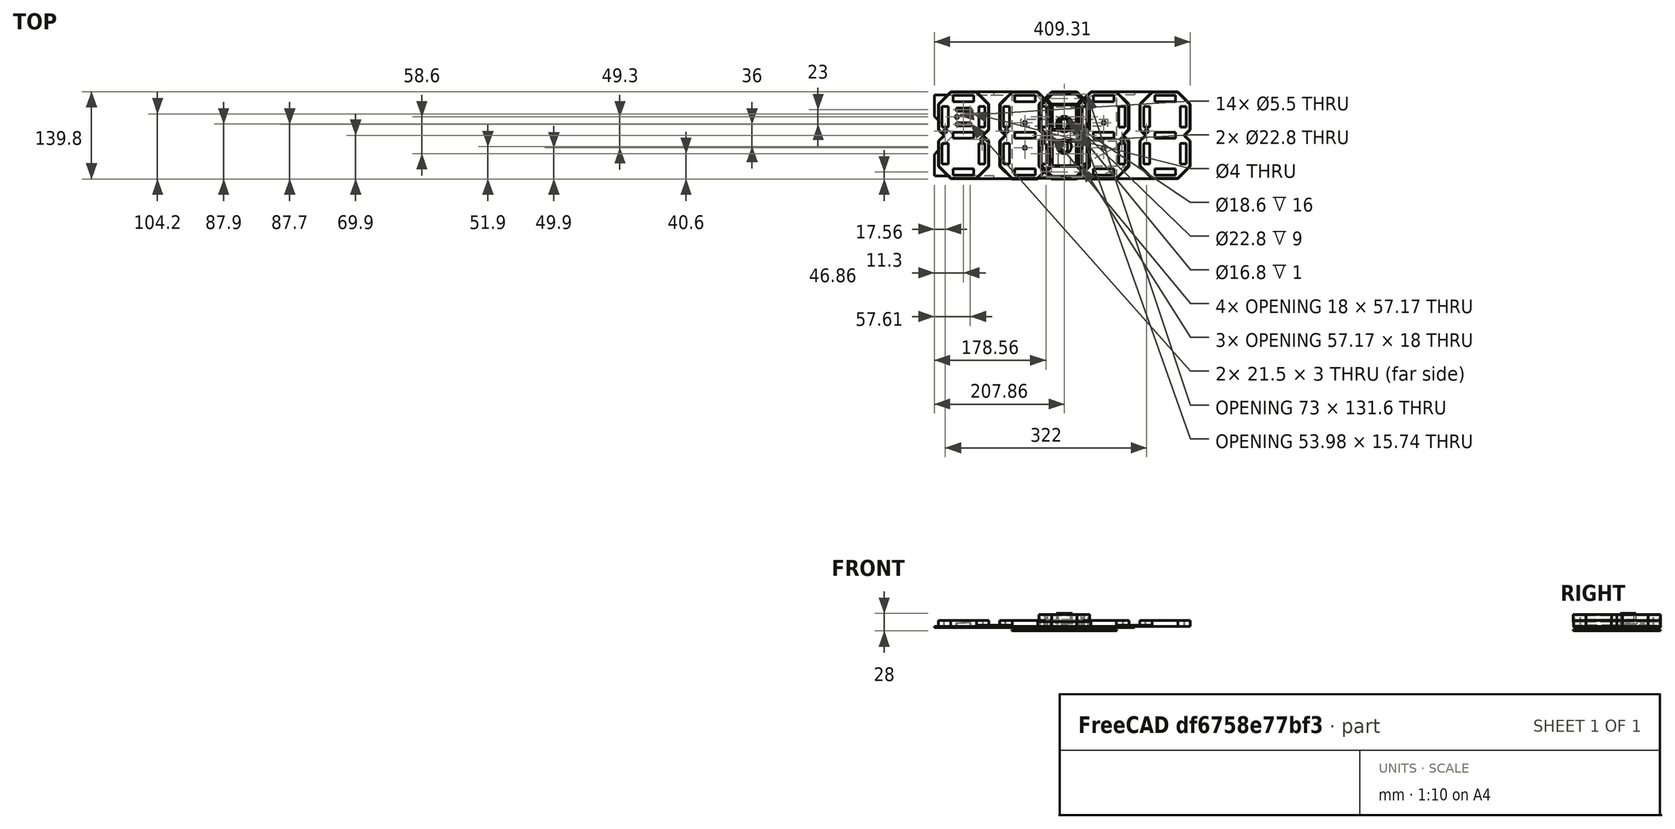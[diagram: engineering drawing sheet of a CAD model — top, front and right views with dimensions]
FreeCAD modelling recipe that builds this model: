
FCSTD DOCUMENT  (FreeCAD 0.19R24291 (Git))
Label: 7-segments-clock-17
License: All rights reserved
LicenseURL: http://en.wikipedia.org/wiki/All_rights_reserved
objects: Sketcher::SketchObject×33, PartDesign::Body×26, PartDesign::Pad×23, PartDesign::ShapeBinder×18, PartDesign::FeatureBase×11, PartDesign::Pocket×10, PartDesign::Thickness×5, Part::MultiFuse×4, PartDesign::Mirrored×4
note: 172 computed .brp shape members not serialized (recipe doc carries the construction recipe); baked Part::Feature solids carry a one-line shape summary decoded from their .brp

FEATURE [Sketcher::SketchObject] Sketch
  FullyConstrained = true
  MapMode = 5
  Support = -> [XY_Plane]
  sketch-geometry (14):
    g0: LineSegment StartX=-30 StartY=0 StartZ=0 EndX=-20 EndY=10 EndZ=0
    g1: LineSegment StartX=-20 StartY=10 StartZ=0 EndX=20 EndY=10 EndZ=0
    g2: LineSegment StartX=20 StartY=10 StartZ=0 EndX=30 EndY=0 EndZ=0
    g3: LineSegment StartX=30 StartY=0 StartZ=0 EndX=20 EndY=-10 EndZ=0
    g4: LineSegment StartX=20 StartY=-10 StartZ=0 EndX=-20 EndY=-10 EndZ=0
    g5: LineSegment StartX=-20 StartY=-10 StartZ=0 EndX=-30 EndY=0 EndZ=0
    g6: LineSegment StartX=-28.5858 StartY=5.3e-15 StartZ=0 EndX=-19.5858 EndY=9 EndZ=0
    g7: LineSegment StartX=-19.5858 StartY=9 StartZ=0 EndX=19.5858 EndY=9 EndZ=0
    g8: LineSegment StartX=19.5858 StartY=9 StartZ=0 EndX=28.5858 EndY=0 EndZ=0
    g9: LineSegment StartX=28.5858 StartY=0 StartZ=0 EndX=19.5858 EndY=-9 EndZ=0
    g10: LineSegment StartX=19.5858 StartY=-9 StartZ=0 EndX=-19.5858 EndY=-9 EndZ=0
    g11: LineSegment StartX=-19.5858 StartY=-9 StartZ=0 EndX=-28.5858 EndY=5.3e-15 EndZ=0
    g12: LineSegment StartX=-10 StartY=9 StartZ=0 EndX=-10 EndY=10 EndZ=0
    g13: LineSegment StartX=24.2426 StartY=4.34315 StartZ=0 EndX=24.9497 EndY=5.05025 EndZ=0
  constraints (41):
    c: PointOnObject(g0,g-1)
    c: Coincident(g0,g1)
    c: Horizontal(g1)
    c: Coincident(g1,g2)
    c: Coincident(g2,g3)
    c: Coincident(g3,g4)
    c: Horizontal(g4)
    c: Coincident(g4,g5)
    c: Coincident(g5,g0)
    c: Angle(g3,g4) = 2.35619
    c: Equal(g4,g1)
    c: Symmetric(g0,g3,g-1)
    c: Symmetric(g2,g0,g-2)
    c: Vertical(g3,g1)
    c: Coincident(g6,g7)
    c: Horizontal(g7)
    c: Coincident(g7,g8)
    c: Coincident(g8,g9)
    c: Coincident(g9,g10)
    c: Horizontal(g10)
    c: Coincident(g10,g11)
    c: Coincident(g11,g6)
    c: Angle(g9,g10) = 2.35619
    c: Equal(g10,g7)
    c: Vertical(g9,g7)
    c: Equal(g11,g6)
    c: Equal(g6,g8)
    c: Equal(g8,g9)
    c: Symmetric(g9,g6,g-1)
    c: PointOnObject(g12,g7)
    c: PointOnObject(g12,g1)
    c: Vertical(g12)
    c: Distance(g12) = 1
    c: PointOnObject(g13,g8)
    c: PointOnObject(g13,g2)
    c: Perpendicular(g13,g8)
    c: Equal(g12,g13)
    c: Distance(g0,g12) = 10
    c: Distance(g13,g1) = 7
    c: DistanceX(g0,g2) = 60
    c: DistanceY(g4,g0) = 20
FEATURE [PartDesign::Pad] Pad
  Direction = (1,1,1)
  Length = 18
  Length2 = 100
  Profile = -> Sketch
  Type = 0
FEATURE [PartDesign::Body] Body  label="original-middle"
  Group = -> [Sketch,Pad]
  Origin = -> Origin
  Tip = -> Pad
FEATURE [PartDesign::FeatureBase] Clone
  BaseFeature = -> Body
FEATURE [PartDesign::Body] Body001
  BaseFeature = -> Body
  Group = -> [Clone]
  Origin = -> Origin001
  Placement = pos=(-29.3,29.3,0) rot=(0,0,1;1.5708rad)
  Tip = -> Clone
FEATURE [PartDesign::FeatureBase] Clone001
  BaseFeature = -> Body
FEATURE [PartDesign::Body] Body002
  BaseFeature = -> Body
  Group = -> [Clone001]
  Origin = -> Origin002
  Placement = pos=(29.3,29.3,0) rot=(0,0,1;1.5708rad)
  Tip = -> Clone001
FEATURE [PartDesign::FeatureBase] Clone002
  BaseFeature = -> Body
FEATURE [PartDesign::Body] Body003
  BaseFeature = -> Body
  Group = -> [Clone002]
  Origin = -> Origin003
  Placement = pos=(0,58.6,0) rot=(0,0,1;0rad)
  Tip = -> Clone002
FEATURE [PartDesign::FeatureBase] Clone003
  BaseFeature = -> Body
FEATURE [PartDesign::Body] Body005
  BaseFeature = -> Body
  Group = -> [Clone003]
  Origin = -> Origin005
  Placement = pos=(-29.3,-29.3,0) rot=(0,0,1;1.5708rad)
  Tip = -> Clone003
FEATURE [PartDesign::FeatureBase] Clone004
  BaseFeature = -> Body
FEATURE [PartDesign::Body] Body006
  Group = -> [Clone004]
  Origin = -> Origin006
  Placement = pos=(0,-58.6,0) rot=(0,0,1;0rad)
  Tip = -> Clone004
FEATURE [PartDesign::FeatureBase] Clone005
  BaseFeature = -> Body
FEATURE [PartDesign::Body] Body007
  BaseFeature = -> Body
  Group = -> [Clone005]
  Origin = -> Origin007
  Placement = pos=(29.3,-29.3,0) rot=(0,0,1;1.5708rad)
  Tip = -> Clone005
FEATURE [Part::MultiFuse] Fusion  label="digit"
  Shapes = -> [Body,Body006,Body005,Body003,Body002,Body001,Body007]
FEATURE [PartDesign::ShapeBinder] ShapeBinder
  Support = -> [Fusion]
  TraceSupport = false
FEATURE [Sketcher::SketchObject] Sketch001
  ExternalGeometry = -> [ShapeBinder]
  FullyConstrained = false
  MapMode = 5
  Support = -> [XY_Plane008]
  sketch-geometry (19):
    g0: LineSegment StartX=-20.4763 StartY=69.75 StartZ=0 EndX=20.4763 EndY=69.75 EndZ=0
    g1: LineSegment StartX=20.4763 StartY=69.75 StartZ=0 EndX=40.45 EndY=49.7763 EndZ=0
    g2: LineSegment StartX=40.45 StartY=49.7763 StartZ=0 EndX=40.45 EndY=8.82365 EndZ=0
    g3: LineSegment StartX=40.45 StartY=8.82365 StartZ=0 EndX=31.6263 EndY=0 EndZ=0
    g4: LineSegment StartX=31.6263 StartY=0 StartZ=0 EndX=40.45 EndY=-8.82365 EndZ=0
    g5: LineSegment StartX=40.45 StartY=-8.82365 StartZ=0 EndX=40.45 EndY=-49.7763 EndZ=0
    g6: LineSegment StartX=40.45 StartY=-49.7763 StartZ=0 EndX=20.4763 EndY=-69.75 EndZ=0
    g7: LineSegment StartX=20.4763 StartY=-69.75 StartZ=0 EndX=-20.4763 EndY=-69.75 EndZ=0
    g8: LineSegment StartX=-20.4763 StartY=-69.75 StartZ=0 EndX=-40.45 EndY=-49.7763 EndZ=0
    g9: LineSegment StartX=-40.45 StartY=-49.7763 StartZ=0 EndX=-40.45 EndY=-8.82365 EndZ=0
    g10: LineSegment StartX=-40.45 StartY=-8.82365 StartZ=0 EndX=-31.6263 EndY=0 EndZ=0
    g11: LineSegment StartX=-31.6263 StartY=0 StartZ=0 EndX=-40.45 EndY=8.82365 EndZ=0
    g12: LineSegment StartX=-40.45 StartY=8.82365 StartZ=0 EndX=-40.45 EndY=49.7763 EndZ=0
    g13: LineSegment StartX=-40.45 StartY=49.7763 StartZ=0 EndX=-20.4763 EndY=69.75 EndZ=0
    g14: LineSegment StartX=-7.19333e+06 StartY=68.6 StartZ=0 EndX=-7.19333e+06 EndY=69.75 EndZ=0
    g15: LineSegment StartX=-7.19333e+06 StartY=-68.6 StartZ=0 EndX=-7.19333e+06 EndY=-69.75 EndZ=0
    g16: LineSegment StartX=-40.45 StartY=-3.5966e+06 StartZ=0 EndX=-39.3 EndY=-3.5966e+06 EndZ=0
    g17: LineSegment StartX=-33.1474 StartY=1.52109 StartZ=0 EndX=-32.3343 EndY=2.33426 EndZ=0
    g18: LineSegment StartX=-39.3 StartY=11.403 StartZ=0 EndX=-40.45 EndY=11.403 EndZ=0
  constraints (55):
    c: Horizontal(g0)
    c: Coincident(g0,g1)
    c: Coincident(g1,g2)
    c: Vertical(g2)
    c: Coincident(g2,g3)
    c: PointOnObject(g3,g-1)
    c: Coincident(g3,g4)
    c: Coincident(g4,g5)
    c: Vertical(g5)
    c: Coincident(g5,g6)
    c: Coincident(g6,g7)
    c: Horizontal(g7)
    c: Coincident(g7,g8)
    c: Coincident(g8,g9)
    c: Vertical(g9)
    c: Coincident(g9,g10)
    c: Coincident(g10,g11)
    c: Coincident(g11,g12)
    c: Vertical(g12)
    c: Coincident(g12,g13)
    c: Coincident(g13,g0)
    c: Equal(g13,g1)
    c: Equal(g1,g6)
    c: Equal(g6,g8)
    c: Equal(g9,g5)
    c: Equal(g5,g7)
    c: Equal(g7,g0)
    c: Equal(g0,g2)
    c: Equal(g2,g12)
    c: Equal(g11,g3)
    c: Vertical(g11,g9)
    c: Vertical(g4,g2)
    c: Symmetric(g3,g10,g-2)
    c: Symmetric(g4,g9,g-2)
    c: Angle(g11) = 2.35619
    c: Equal(g11,g10)
    c: PointOnObject(g14,g-3)
    c: Vertical(g14)
    c: PointOnObject(g15,g-12)
    c: PointOnObject(g15,g7)
    c: Vertical(g15)
    c: Equal(g15,g14)
    c: PointOnObject(g16,g12)
    c: PointOnObject(g16,g-5)
    c: Horizontal(g16)
    c: Equal(g14,g16)
    c: Angle(g13) = 0.785398
    c: PointOnObject(g17,g11)
    c: PointOnObject(g17,g-6)
    c: PointOnObject(g18,g-5)
    c: PointOnObject(g18,g12)
    c: Horizontal(g18)
    c: Perpendicular(g-6,g17)
    c: Equal(g17,g18)
    c: DistanceX(g18,g18) = 1.15
FEATURE [PartDesign::Pad] Pad001
  Direction = (1,1,1)
  Length = 10
  Length2 = 100
  Profile = -> Sketch001
  Type = 0
FEATURE [PartDesign::Thickness] Thickness
  Base = -> Pad001 [Face16]
  BaseFeature = -> Pad001
  Intersection = false
  Join = 0
  Mode = 0
  Reversed = true
  SupportTransform = false
  Value = 1
FEATURE [Sketcher::SketchObject] Sketch002
  ExternalGeometry = -> [ShapeBinder]
  FullyConstrained = true
  MapMode = 5
  Placement = pos=(0,0,1) rot=(0,0,1;0rad)
  Support = -> [Thickness]
  sketch-geometry (34):
    g0: LineSegment StartX=-29.3 StartY=48.8858 StartZ=0 EndX=-29.3 EndY=-48.8858 EndZ=0
    g1: LineSegment StartX=29.3 StartY=48.8858 StartZ=0 EndX=29.3 EndY=-48.8858 EndZ=0
    g2: LineSegment StartX=-19.5858 StartY=58.6 StartZ=0 EndX=19.5858 EndY=58.6 EndZ=0
    g3: LineSegment StartX=-19.5858 StartY=-58.6 StartZ=0 EndX=19.5858 EndY=-58.6 EndZ=0
    g4: LineSegment StartX=-16.5 StartY=63.6 StartZ=0 EndX=16.5 EndY=63.6 EndZ=0
    g5: LineSegment StartX=16.5 StartY=63.6 StartZ=0 EndX=16.5 EndY=53.6 EndZ=0
    g6: LineSegment StartX=16.5 StartY=53.6 StartZ=0 EndX=-16.5 EndY=53.6 EndZ=0
    g7: LineSegment StartX=-16.5 StartY=53.6 StartZ=0 EndX=-16.5 EndY=63.6 EndZ=0
    g8: LineSegment StartX=24.3 StartY=45.8 StartZ=0 EndX=34.3 EndY=45.8 EndZ=0
    g9: LineSegment StartX=34.3 StartY=45.8 StartZ=0 EndX=34.3 EndY=12.8 EndZ=0
    g10: LineSegment StartX=34.3 StartY=12.8 StartZ=0 EndX=24.3 EndY=12.8 EndZ=0
    g11: LineSegment StartX=24.3 StartY=12.8 StartZ=0 EndX=24.3 EndY=45.8 EndZ=0
    g12: LineSegment StartX=24.3 StartY=-12.8 StartZ=0 EndX=34.3 EndY=-12.8 EndZ=0
    g13: LineSegment StartX=34.3 StartY=-12.8 StartZ=0 EndX=34.3 EndY=-45.8 EndZ=0
    g14: LineSegment StartX=34.3 StartY=-45.8 StartZ=0 EndX=24.3 EndY=-45.8 EndZ=0
    g15: LineSegment StartX=24.3 StartY=-45.8 StartZ=0 EndX=24.3 EndY=-12.8 EndZ=0
    g16: LineSegment StartX=-34.3 StartY=-12.8 StartZ=0 EndX=-24.3 EndY=-12.8 EndZ=0
    g17: LineSegment StartX=-24.3 StartY=-12.8 StartZ=0 EndX=-24.3 EndY=-45.8 EndZ=0
    g18: LineSegment StartX=-24.3 StartY=-45.8 StartZ=0 EndX=-34.3 EndY=-45.8 EndZ=0
    g19: LineSegment StartX=-34.3 StartY=-45.8 StartZ=0 EndX=-34.3 EndY=-12.8 EndZ=0
    g20: LineSegment StartX=-16.5 StartY=-53.6 StartZ=0 EndX=16.5 EndY=-53.6 EndZ=0
    g21: LineSegment StartX=16.5 StartY=-53.6 StartZ=0 EndX=16.5 EndY=-63.6 EndZ=0
    g22: LineSegment StartX=16.5 StartY=-63.6 StartZ=0 EndX=-16.5 EndY=-63.6 EndZ=0
    g23: LineSegment StartX=-16.5 StartY=-63.6 StartZ=0 EndX=-16.5 EndY=-53.6 EndZ=0
    g24: LineSegment StartX=-34.3 StartY=45.8 StartZ=0 EndX=-24.3 EndY=45.8 EndZ=0
    g25: LineSegment StartX=-24.3 StartY=45.8 StartZ=0 EndX=-24.3 EndY=12.8 EndZ=0
    g26: LineSegment StartX=-24.3 StartY=12.8 StartZ=0 EndX=-34.3 EndY=12.8 EndZ=0
    g27: LineSegment StartX=-34.3 StartY=12.8 StartZ=0 EndX=-34.3 EndY=45.8 EndZ=0
    g28: LineSegment StartX=-16.5 StartY=5 StartZ=0 EndX=16.5 EndY=5 EndZ=0
    g29: LineSegment StartX=16.5 StartY=5 StartZ=0 EndX=16.5 EndY=-5 EndZ=0
    g30: LineSegment StartX=16.5 StartY=-5 StartZ=0 EndX=-16.5 EndY=-5 EndZ=0
    g31: LineSegment StartX=-16.5 StartY=-5 StartZ=0 EndX=-16.5 EndY=5 EndZ=0
    g32: LineSegment StartX=-38.3 StartY=-29.3 StartZ=0 EndX=38.3 EndY=-29.3 EndZ=0
    g33: LineSegment StartX=38.3 StartY=29.3 StartZ=0 EndX=-38.3 EndY=29.3 EndZ=0
  constraints (93):
    c: Symmetric(g-6,g-5,g0)
    c: Symmetric(g-4,g-3,g1)
    c: Horizontal(g1,g0)
    c: Horizontal(g0,g-6)
    c: Horizontal(g-14,g0)
    c: Horizontal(g0,g1)
    c: Horizontal(g2)
    c: Vertical(g3,g-16)
    c: Vertical(g3,g-15)
    c: Vertical(g-15,g2)
    c: Symmetric(g-15,g-16,g3)
    c: Symmetric(g-8,g-7,g2)
    c: Coincident(g4,g5)
    c: Coincident(g5,g6)
    c: Coincident(g6,g7)
    c: Coincident(g7,g4)
    c: Horizontal(g4)
    c: Horizontal(g6)
    c: Vertical(g7)
    c: Coincident(g8,g9)
    c: Coincident(g9,g10)
    c: Coincident(g10,g11)
    c: Coincident(g11,g8)
    c: Horizontal(g10)
    c: Vertical(g9)
    c: Coincident(g12,g13)
    c: Coincident(g13,g14)
    c: Coincident(g14,g15)
    c: Coincident(g15,g12)
    c: Horizontal(g12)
    c: Horizontal(g14)
    c: Vertical(g13)
    c: Vertical(g15)
    c: Coincident(g16,g17)
    c: Coincident(g17,g18)
    c: Coincident(g18,g19)
    c: Coincident(g19,g16)
    c: Horizontal(g16)
    c: Horizontal(g18)
    c: Vertical(g17)
    c: Coincident(g20,g21)
    c: Coincident(g21,g22)
    c: Coincident(g22,g23)
    c: Coincident(g23,g20)
    c: Horizontal(g22)
    c: Vertical(g21)
    c: DistanceX(g4,g4) = 33
    c: DistanceY(g7,g7) = 10
    c: Coincident(g24,g25)
    c: Coincident(g25,g26)
    c: Coincident(g26,g27)
    c: Coincident(g27,g24)
    c: Horizontal(g24)
    c: Vertical(g25)
    c: Vertical(g27)
    c: Equal(g6,g25)
    c: Equal(g25,g11)
    c: Equal(g11,g15)
    c: Equal(g15,g17)
    c: Equal(g17,g20)
    c: Equal(g7,g24)
    c: Equal(g24,g8)
    c: Equal(g8,g12)
    c: Equal(g12,g16)
    c: Equal(g16,g21)
    c: Coincident(g28,g29)
    c: Coincident(g29,g30)
    c: Coincident(g30,g31)
    c: Coincident(g31,g28)
    c: Horizontal(g30)
    c: Vertical(g29)
    c: Equal(g28,g4)
    c: Equal(g7,g31)
    c: Symmetric(g8,g8,g1)
    c: Vertical(g10,g12)
    c: Symmetric(g26,g25,g0)
    c: Vertical(g25,g16)
    c: Symmetric(g20,g22,g3)
    c: Symmetric(g20,g20,g-2)
    c: Vertical(g20,g5)
    c: Symmetric(g5,g4,g2)
    c: PointOnObject(g32,g-14)
    c: PointOnObject(g32,g-12)
    c: PointOnObject(g33,g-3)
    c: PointOnObject(g33,g-6)
    c: Symmetric(g-14,g-14,g32)
    c: Symmetric(g-6,g-6,g33)
    c: Symmetric(g8,g10,g33)
    c: Horizontal(g8,g24)
    c: Symmetric(g16,g18,g32)
    c: Horizontal(g16,g12)
    c: Symmetric(g28,g28,g-2)
    c: Symmetric(g30,g28,g-1)
FEATURE [PartDesign::Pad] Pad002
  BaseFeature = -> Thickness
  Direction = (1,1,1)
  Length = 0.3
  Length2 = 100
  Profile = -> Sketch002
  Type = 0
FEATURE [Sketcher::SketchObject] Sketch003
  ExternalGeometry = -> [ShapeBinder]
  FullyConstrained = true
  MapMode = 5
  Placement = pos=(0,0,1) rot=(0,0,1;0rad)
  Support = -> [Pad002]
  sketch-geometry (13):
    g0: LineSegment StartX=-19.3 StartY=29.3 StartZ=0 EndX=19.3 EndY=29.3 EndZ=0
    g1: Circle CenterX=-29.3 CenterY=6.71421 CenterZ=0 NormalX=0 NormalY=0 NormalZ=1 AngleXU=0 Radius=2.75
    g2: Circle CenterX=-10.75 CenterY=29.3 CenterZ=0 NormalX=0 NormalY=0 NormalZ=1 AngleXU=0 Radius=2.75
    g3: Circle CenterX=10.75 CenterY=34.3 CenterZ=0 NormalX=0 NormalY=0 NormalZ=1 AngleXU=0 Radius=2
    g4: Circle CenterX=29.3 CenterY=-6.71421 CenterZ=0 NormalX=0 NormalY=0 NormalZ=1 AngleXU=0 Radius=2.75
    g5: LineSegment StartX=-10.75 StartY=42.3 StartZ=0 EndX=10.75 EndY=42.3 EndZ=0
    g6: LineSegment StartX=10.75 StartY=42.3 StartZ=0 EndX=10.75 EndY=39.3 EndZ=0
    g7: LineSegment StartX=10.75 StartY=39.3 StartZ=0 EndX=-10.75 EndY=39.3 EndZ=0
    g8: LineSegment StartX=-10.75 StartY=39.3 StartZ=0 EndX=-10.75 EndY=42.3 EndZ=0
    g9: LineSegment StartX=-10.75 StartY=19.3 StartZ=0 EndX=10.75 EndY=19.3 EndZ=0
    g10: LineSegment StartX=10.75 StartY=19.3 StartZ=0 EndX=10.75 EndY=16.3 EndZ=0
    g11: LineSegment StartX=10.75 StartY=16.3 StartZ=0 EndX=-10.75 EndY=16.3 EndZ=0
    g12: LineSegment StartX=-10.75 StartY=16.3 StartZ=0 EndX=-10.75 EndY=19.3 EndZ=0
  constraints (38):
    c: Vertical(g0,g-3)
    c: Vertical(g0,g-3)
    c: Symmetric(g-3,g-4,g0)
    c: Radius(g1) = 2.75
    c: Equal(g1,g2)
    c: Equal(g2,g4)
    c: Radius(g3) = 2
    c: Coincident(g5,g6)
    c: Coincident(g6,g7)
    c: Coincident(g7,g8)
    c: Coincident(g8,g5)
    c: Horizontal(g5)
    c: Horizontal(g7)
    c: Vertical(g6)
    c: Vertical(g8)
    c: Coincident(g9,g10)
    c: Coincident(g10,g11)
    c: Coincident(g11,g12)
    c: Coincident(g12,g9)
    c: Horizontal(g11)
    c: Vertical(g10)
    c: Vertical(g12)
    c: Equal(g9,g7)
    c: Equal(g6,g10)
    c: Vertical(g1,g-6)
    c: Distance(g1,g-6) = 6
    c: Vertical(g4,g-8)
    c: Distance(g4,g-8) = 6
    c: DistanceY(g9,g0) = 10
    c: DistanceY(g0,g6) = 10
    c: Symmetric(g9,g9,g-2)
    c: Vertical(g6,g9)
    c: DistanceX(g5,g5) = 21.5
    c: DistanceY(g8,g8) = 3
    c: PointOnObject(g2,g0)
    c: Vertical(g3,g6)
    c: Vertical(g2,g7)
    c: DistanceY(g0,g3) = 5
FEATURE [PartDesign::Pocket] Pocket
  BaseFeature = -> Pad002
  Length = 5
  Length2 = 100
  Profile = -> Sketch003
  Type = 1
FEATURE [Sketcher::SketchObject] Sketch004
  ExternalGeometry = -> [Pocket]
  FullyConstrained = true
  MapMode = 5
  Placement = pos=(0,0,1) rot=(0,0,1;0rad)
  Support = -> [Pocket]
  sketch-geometry (16):
    g0: LineSegment StartX=-10.75 StartY=42.3 StartZ=0 EndX=10.75 EndY=42.3 EndZ=0
    g1: LineSegment StartX=10.75 StartY=42.3 StartZ=0 EndX=10.75 EndY=39.3 EndZ=0
    g2: LineSegment StartX=10.75 StartY=39.3 StartZ=0 EndX=-10.75 EndY=39.3 EndZ=0
    g3: LineSegment StartX=-10.75 StartY=39.3 StartZ=0 EndX=-10.75 EndY=42.3 EndZ=0
    g4: LineSegment StartX=-10.75 StartY=19.3 StartZ=0 EndX=10.75 EndY=19.3 EndZ=0
    g5: LineSegment StartX=10.75 StartY=19.3 StartZ=0 EndX=10.75 EndY=16.3 EndZ=0
    g6: LineSegment StartX=10.75 StartY=16.3 StartZ=0 EndX=-10.75 EndY=16.3 EndZ=0
    g7: LineSegment StartX=-10.75 StartY=16.3 StartZ=0 EndX=-10.75 EndY=19.3 EndZ=0
    g8: LineSegment StartX=-11.75 StartY=43.3 StartZ=0 EndX=11.75 EndY=43.3 EndZ=0
    g9: LineSegment StartX=11.75 StartY=43.3 StartZ=0 EndX=11.75 EndY=38.3 EndZ=0
    g10: LineSegment StartX=11.75 StartY=38.3 StartZ=0 EndX=-11.75 EndY=38.3 EndZ=0
    g11: LineSegment StartX=-11.75 StartY=38.3 StartZ=0 EndX=-11.75 EndY=43.3 EndZ=0
    g12: LineSegment StartX=-11.75 StartY=20.3 StartZ=0 EndX=11.75 EndY=20.3 EndZ=0
    g13: LineSegment StartX=11.75 StartY=20.3 StartZ=0 EndX=11.75 EndY=15.3 EndZ=0
    g14: LineSegment StartX=11.75 StartY=15.3 StartZ=0 EndX=-11.75 EndY=15.3 EndZ=0
    g15: LineSegment StartX=-11.75 StartY=15.3 StartZ=0 EndX=-11.75 EndY=20.3 EndZ=0
  constraints (42):
    c: Coincident(g0,g1)
    c: Coincident(g1,g2)
    c: Coincident(g2,g3)
    c: Coincident(g3,g0)
    c: Horizontal(g0)
    c: Horizontal(g2)
    c: Vertical(g1)
    c: Vertical(g3)
    c: Coincident(g0,g-3)
    c: Coincident(g1,g-4)
    c: Coincident(g4,g5)
    c: Coincident(g5,g6)
    c: Coincident(g6,g7)
    c: Coincident(g7,g4)
    c: Horizontal(g4)
    c: Horizontal(g6)
    c: Vertical(g5)
    c: Vertical(g7)
    c: Coincident(g4,g-5)
    c: Coincident(g5,g-6)
    c: Coincident(g8,g9)
    c: Coincident(g9,g10)
    c: Coincident(g10,g11)
    c: Coincident(g11,g8)
    c: Horizontal(g8)
    c: Vertical(g9)
    c: Vertical(g11)
    c: Coincident(g12,g13)
    c: Coincident(g13,g14)
    c: Coincident(g14,g15)
    c: Coincident(g15,g12)
    c: Horizontal(g14)
    c: Vertical(g13)
    c: Vertical(g15)
    c: Equal(g12,g10)
    c: Equal(g9,g13)
    c: Symmetric(g12,g12,g-2)
    c: Symmetric(g10,g9,g-2)
    c: DistanceY(g0,g8) = 1
    c: DistanceY(g9,g1) = 1
    c: DistanceX(g1,g9) = 1
    c: DistanceY(g4,g12) = 1
FEATURE [PartDesign::Pad] Pad003
  BaseFeature = -> Pocket
  Direction = (1,1,1)
  Length = 5
  Length2 = 100
  Profile = -> Sketch004
  Type = 0
FEATURE [PartDesign::Body] Body008  label="back-esp"
  Group = -> [ShapeBinder,Sketch001,Pad001,Thickness,Sketch002,Pad002,Sketch003,Pocket,Sketch004,Pad003]
  Origin = -> Origin008
  Tip = -> Pad003
FEATURE [PartDesign::ShapeBinder] ShapeBinder001
  Support = -> [Body]
  TraceSupport = false
FEATURE [Sketcher::SketchObject] Sketch005
  ExternalGeometry = -> [ShapeBinder001]
  FullyConstrained = false
  MapMode = 5
  Support = -> [XY_Plane009]
  sketch-geometry (8):
    g0: LineSegment StartX=-19.5319 StartY=8.87 StartZ=0 EndX=19.5319 EndY=8.87 EndZ=0
    g1: LineSegment StartX=19.5319 StartY=8.87 StartZ=0 EndX=28.4019 EndY=0 EndZ=0
    g2: LineSegment StartX=28.4019 StartY=0 StartZ=0 EndX=19.5319 EndY=-8.87 EndZ=0
    g3: LineSegment StartX=19.5319 StartY=-8.87 StartZ=0 EndX=-19.5319 EndY=-8.87 EndZ=0
    g4: LineSegment StartX=-19.5319 StartY=-8.87 StartZ=0 EndX=-28.4019 EndY=0 EndZ=0
    g5: LineSegment StartX=-28.4019 StartY=0 StartZ=0 EndX=-19.5319 EndY=8.87 EndZ=0
    g6: LineSegment StartX=6.84283 StartY=8.87 StartZ=0 EndX=6.84283 EndY=9 EndZ=0
    g7: LineSegment StartX=22.9862 StartY=5.41571 StartZ=0 EndX=23.0782 EndY=5.50763 EndZ=0
  constraints (21):
    c: Coincident(g0,g1)
    c: PointOnObject(g1,g-1)
    c: Coincident(g1,g2)
    c: Coincident(g2,g3)
    c: Horizontal(g3)
    c: Coincident(g3,g4)
    c: Coincident(g4,g5)
    c: Equal(g0,g3)
    c: Symmetric(g4,g1,g-2)
    c: Symmetric(g2,g0,g-1)
    c: Angle(g5) = 0.785398
    c: PointOnObject(g6,g0)
    c: PointOnObject(g6,g-3)
    c: Vertical(g6)
    c: DistanceY(g6,g6) = 0.13
    c: PointOnObject(g7,g1)
    c: PointOnObject(g7,g-7)
    c: Perpendicular(g1,g7)
    c: Equal(g7,g6)
    c: Coincident(g0,g5)
    c: Symmetric(g0,g0,g-2)
FEATURE [PartDesign::Pad] Pad004
  Direction = (1,1,1)
  Length = 18
  Length2 = 100
  Profile = -> Sketch005
  Type = 0
FEATURE [Sketcher::SketchObject] Sketch006
  ExternalGeometry = -> [Pad004]
  FullyConstrained = false
  MapMode = 5
  Placement = pos=(0,0,18) rot=(0,0,1;0rad)
  Support = -> [Pad004]
  sketch-geometry (8):
    g0: LineSegment StartX=-19.1177 StartY=7.87 StartZ=0 EndX=19.1177 EndY=7.87 EndZ=0
    g1: LineSegment StartX=19.1177 StartY=7.87 StartZ=0 EndX=26.9877 EndY=-9e-16 EndZ=0
    g2: LineSegment StartX=26.9877 StartY=0 StartZ=0 EndX=19.1177 EndY=-7.87 EndZ=0
    g3: LineSegment StartX=19.1177 StartY=-7.87 StartZ=0 EndX=-19.1177 EndY=-7.87 EndZ=0
    g4: LineSegment StartX=-19.1177 StartY=-7.87 StartZ=0 EndX=-26.9877 EndY=-9e-16 EndZ=0
    g5: LineSegment StartX=-26.9877 StartY=0 StartZ=0 EndX=-19.1177 EndY=7.87 EndZ=0
    g6: LineSegment StartX=5.64393 StartY=7.87 StartZ=0 EndX=5.64393 EndY=8.87 EndZ=0
    g7: LineSegment StartX=23.5274 StartY=3.46031 StartZ=0 EndX=24.2345 EndY=4.16742 EndZ=0
  constraints (22):
    c: Horizontal(g0)
    c: Coincident(g0,g1)
    c: PointOnObject(g1,g-1)
    c: Coincident(g1,g2)
    c: Coincident(g2,g3)
    c: Horizontal(g3)
    c: Coincident(g3,g4)
    c: Coincident(g4,g5)
    c: Coincident(g5,g0)
    c: Symmetric(g1,g4,g-2)
    c: Symmetric(g2,g0,g-1)
    c: Equal(g2,g5)
    c: Angle(g5) = 0.785398
    c: Vertical(g0,g3)
    c: PointOnObject(g6,g0)
    c: PointOnObject(g6,g-3)
    c: Vertical(g6)
    c: PointOnObject(g7,g1)
    c: PointOnObject(g7,g-8)
    c: Perpendicular(g1,g7)
    c: Equal(g6,g7)
    c: DistanceY(g6,g6) = 1
FEATURE [PartDesign::Pocket] Pocket001
  BaseFeature = -> Pad004
  Length = 5
  Length2 = 100
  Profile = -> Sketch006
  Type = 1
FEATURE [PartDesign::Body] Body009  label="single-segment"
  Group = -> [ShapeBinder001,Sketch005,Pad004,Sketch006,Pocket001]
  Origin = -> Origin009
  Tip = -> Pocket001
FEATURE [PartDesign::ShapeBinder] ShapeBinder002
  Support = -> [Fusion]
  TraceSupport = false
FEATURE [Sketcher::SketchObject] Sketch008
  ExternalGeometry = -> [ShapeBinder002]
  FullyConstrained = false
  MapMode = 5
  Support = -> [XY_Plane017]
  sketch-geometry (19):
    g0: LineSegment StartX=-20.4971 StartY=69.8 StartZ=0 EndX=20.4971 EndY=69.8 EndZ=0
    g1: LineSegment StartX=20.4971 StartY=69.8 StartZ=0 EndX=40.5 EndY=49.7971 EndZ=0
    g2: LineSegment StartX=40.5 StartY=49.7971 StartZ=0 EndX=40.5 EndY=8.80294 EndZ=0
    g3: LineSegment StartX=40.5 StartY=8.80294 StartZ=0 EndX=31.6971 EndY=0 EndZ=0
    g4: LineSegment StartX=31.6971 StartY=0 StartZ=0 EndX=40.5 EndY=-8.80294 EndZ=0
    g5: LineSegment StartX=40.5 StartY=-8.80294 StartZ=0 EndX=40.5 EndY=-49.7971 EndZ=0
    g6: LineSegment StartX=40.5 StartY=-49.7971 StartZ=0 EndX=20.4971 EndY=-69.8 EndZ=0
    g7: LineSegment StartX=20.4971 StartY=-69.8 StartZ=0 EndX=-20.4971 EndY=-69.8 EndZ=0
    g8: LineSegment StartX=-20.4971 StartY=-69.8 StartZ=0 EndX=-40.5 EndY=-49.7971 EndZ=0
    g9: LineSegment StartX=-40.5 StartY=-49.7971 StartZ=0 EndX=-40.5 EndY=-8.80294 EndZ=0
    g10: LineSegment StartX=-40.5 StartY=-8.80294 StartZ=0 EndX=-31.6971 EndY=0 EndZ=0
    g11: LineSegment StartX=-31.6971 StartY=0 StartZ=0 EndX=-40.5 EndY=8.80294 EndZ=0
    g12: LineSegment StartX=-40.5 StartY=8.80294 StartZ=0 EndX=-40.5 EndY=49.7971 EndZ=0
    g13: LineSegment StartX=-40.5 StartY=49.7971 StartZ=0 EndX=-20.4971 EndY=69.8 EndZ=0
    g14: LineSegment StartX=-7.19333e+06 StartY=68.6 StartZ=0 EndX=-7.19333e+06 EndY=69.8 EndZ=0
    g15: LineSegment StartX=-7.19333e+06 StartY=-68.6 StartZ=0 EndX=-7.19333e+06 EndY=-69.8 EndZ=0
    g16: LineSegment StartX=-40.5 StartY=-3.5966e+06 StartZ=0 EndX=-39.3 EndY=-3.5966e+06 EndZ=0
    g17: LineSegment StartX=34.9315 StartY=3.23442 StartZ=0 EndX=34.083 EndY=4.08295 EndZ=0
    g18: LineSegment StartX=40.5 StartY=11.0092 StartZ=0 EndX=39.3 EndY=11.0092 EndZ=0
  constraints (55):
    c: Horizontal(g0)
    c: Coincident(g0,g1)
    c: Coincident(g1,g2)
    c: Vertical(g2)
    c: Coincident(g2,g3)
    c: PointOnObject(g3,g-1)
    c: Coincident(g3,g4)
    c: Coincident(g4,g5)
    c: Vertical(g5)
    c: Coincident(g5,g6)
    c: Coincident(g6,g7)
    c: Horizontal(g7)
    c: Coincident(g7,g8)
    c: Coincident(g8,g9)
    c: Vertical(g9)
    c: Coincident(g9,g10)
    c: Coincident(g10,g11)
    c: Coincident(g11,g12)
    c: Vertical(g12)
    c: Coincident(g12,g13)
    c: Coincident(g13,g0)
    c: Equal(g13,g1)
    c: Equal(g1,g6)
    c: Equal(g6,g8)
    c: Equal(g9,g5)
    c: Equal(g5,g7)
    c: Equal(g7,g0)
    c: Equal(g0,g2)
    c: Equal(g2,g12)
    c: Equal(g11,g3)
    c: Vertical(g11,g9)
    c: Vertical(g4,g2)
    c: Symmetric(g3,g10,g-2)
    c: Symmetric(g4,g9,g-2)
    c: Angle(g11) = 2.35619
    c: Equal(g11,g10)
    c: PointOnObject(g14,g-3)
    c: Vertical(g14)
    c: PointOnObject(g15,g-12)
    c: PointOnObject(g15,g7)
    c: Vertical(g15)
    c: Equal(g15,g14)
    c: PointOnObject(g16,g12)
    c: PointOnObject(g16,g-5)
    c: Horizontal(g16)
    c: Equal(g14,g16)
    c: Angle(g13) = 0.785398
    c: PointOnObject(g17,g3)
    c: PointOnObject(g18,g2)
    c: Horizontal(g18)
    c: Perpendicular(g-9,g17)
    c: Equal(g18,g17)
    c: PointOnObject(g18,g-4)
    c: PointOnObject(g17,g-9)
    c: DistanceX(g18,g18) = 1.2
FEATURE [PartDesign::Pad] Pad006
  Direction = (1,1,1)
  Length = 11.5
  Length2 = 100
  Profile = -> Sketch008
  Type = 0
FEATURE [PartDesign::Thickness] Thickness001
  Base = -> Pad006 [Face16]
  BaseFeature = -> Pad006
  Intersection = false
  Join = 0
  Mode = 0
  Reversed = true
  SupportTransform = false
  Value = 1
FEATURE [Sketcher::SketchObject] Sketch009
  ExternalGeometry = -> [Thickness001]
  FullyConstrained = false
  MapMode = 5
  Placement = pos=(0,0,1) rot=(0,0,1;0rad)
  Support = -> [Thickness001]
  sketch-geometry (17):
    g0: LineSegment StartX=-18.8402 StartY=65.8 StartZ=0 EndX=18.8402 EndY=65.8 EndZ=0
    g1: LineSegment StartX=18.8402 StartY=65.8 StartZ=0 EndX=36.5 EndY=48.1402 EndZ=0
    g2: LineSegment StartX=36.5 StartY=48.1402 StartZ=0 EndX=36.5 EndY=10.4598 EndZ=0
    g3: LineSegment StartX=36.5 StartY=10.4598 StartZ=0 EndX=26.0402 EndY=0 EndZ=0
    g4: LineSegment StartX=26.0402 StartY=0 StartZ=0 EndX=36.5 EndY=-10.4598 EndZ=0
    g5: LineSegment StartX=36.5 StartY=-10.4598 StartZ=0 EndX=36.5 EndY=-48.1402 EndZ=0
    g6: LineSegment StartX=36.5 StartY=-48.1402 StartZ=0 EndX=18.8402 EndY=-65.8 EndZ=0
    g7: LineSegment StartX=18.8402 StartY=-65.8 StartZ=0 EndX=-18.8402 EndY=-65.8 EndZ=0
    g8: LineSegment StartX=-18.8402 StartY=-65.8 StartZ=0 EndX=-36.5 EndY=-48.1402 EndZ=0
    g9: LineSegment StartX=-36.5 StartY=-48.1402 StartZ=0 EndX=-36.5 EndY=-10.4598 EndZ=0
    g10: LineSegment StartX=-36.5 StartY=-10.4598 StartZ=0 EndX=-26.0402 EndY=0 EndZ=0
    g11: LineSegment StartX=-26.0402 StartY=0 StartZ=0 EndX=-36.5 EndY=10.4598 EndZ=0
    g12: LineSegment StartX=-36.5 StartY=10.4598 StartZ=0 EndX=-36.5 EndY=48.1402 EndZ=0
    g13: LineSegment StartX=-36.5 StartY=48.1402 StartZ=0 EndX=-18.8402 EndY=65.8 EndZ=0
    g14: LineSegment StartX=36.5 StartY=19.7121 StartZ=0 EndX=39.5 EndY=19.7121 EndZ=0
    g15: LineSegment StartX=32.3726 StartY=6.33239 StartZ=0 EndX=34.4939 EndY=4.21107 EndZ=0
    g16: LineSegment StartX=4.90979 StartY=65.8 StartZ=0 EndX=4.90979 EndY=68.8 EndZ=0
  constraints (48):
    c: Horizontal(g0)
    c: Coincident(g0,g1)
    c: Coincident(g1,g2)
    c: Vertical(g2)
    c: Coincident(g2,g3)
    c: PointOnObject(g3,g-1)
    c: Coincident(g3,g4)
    c: Coincident(g4,g5)
    c: Vertical(g5)
    c: Coincident(g5,g6)
    c: Coincident(g6,g7)
    c: Horizontal(g7)
    c: Coincident(g7,g8)
    c: Coincident(g8,g9)
    c: Vertical(g9)
    c: Coincident(g9,g10)
    c: Coincident(g10,g11)
    c: Coincident(g11,g12)
    c: Vertical(g12)
    c: Coincident(g12,g13)
    c: Coincident(g13,g0)
    c: Equal(g5,g2)
    c: Equal(g2,g0)
    c: Equal(g0,g12)
    c: Equal(g12,g9)
    c: Equal(g9,g7)
    c: Equal(g8,g6)
    c: Equal(g6,g1)
    c: Equal(g1,g13)
    c: Angle(g13) = 0.785398
    c: Symmetric(g10,g3,g-2)
    c: Symmetric(g9,g4,g-2)
    c: Vertical(g9,g11)
    c: Horizontal(g1,g12)
    c: Symmetric(g4,g2,g-1)
    c: Angle(g10) = 0.785398
    c: PointOnObject(g14,g2)
    c: PointOnObject(g14,g-13)
    c: Horizontal(g14)
    c: PointOnObject(g15,g3)
    c: PointOnObject(g15,g-12)
    c: Perpendicular(g-12,g15)
    c: Equal(g15,g14)
    c: Distance(g14) = 3
    c: PointOnObject(g16,g0)
    c: PointOnObject(g16,g-3)
    c: Vertical(g16)
    c: Equal(g16,g14)
FEATURE [PartDesign::Pocket] Pocket002
  BaseFeature = -> Thickness001
  Length = 5
  Length2 = 100
  Profile = -> Sketch009
  Type = 0
FEATURE [PartDesign::Body] Body017  label="cover"
  Group = -> [ShapeBinder002,Sketch008,Pad006,Thickness001,Sketch009,Pocket002]
  Origin = -> Origin017
  Placement = pos=(-2e-15,0,19) rot=(0,1,0;3.14159rad)
  Tip = -> Pocket002
FEATURE [PartDesign::ShapeBinder] ShapeBinder003
  Support = -> [Fusion]
  TraceSupport = false
FEATURE [Sketcher::SketchObject] Sketch011
  ExternalGeometry = -> [ShapeBinder003]
  FullyConstrained = false
  MapMode = 5
  Support = -> [XY_Plane025]
  sketch-geometry (19):
    g0: LineSegment StartX=-20.4763 StartY=69.75 StartZ=0 EndX=20.4763 EndY=69.75 EndZ=0
    g1: LineSegment StartX=20.4763 StartY=69.75 StartZ=0 EndX=40.45 EndY=49.7763 EndZ=0
    g2: LineSegment StartX=40.45 StartY=49.7763 StartZ=0 EndX=40.45 EndY=8.82365 EndZ=0
    g3: LineSegment StartX=40.45 StartY=8.82365 StartZ=0 EndX=31.6263 EndY=0 EndZ=0
    g4: LineSegment StartX=31.6263 StartY=0 StartZ=0 EndX=40.45 EndY=-8.82365 EndZ=0
    g5: LineSegment StartX=40.45 StartY=-8.82365 StartZ=0 EndX=40.45 EndY=-49.7763 EndZ=0
    g6: LineSegment StartX=40.45 StartY=-49.7763 StartZ=0 EndX=20.4763 EndY=-69.75 EndZ=0
    g7: LineSegment StartX=20.4763 StartY=-69.75 StartZ=0 EndX=-20.4763 EndY=-69.75 EndZ=0
    g8: LineSegment StartX=-20.4763 StartY=-69.75 StartZ=0 EndX=-40.45 EndY=-49.7763 EndZ=0
    g9: LineSegment StartX=-40.45 StartY=-49.7763 StartZ=0 EndX=-40.45 EndY=-8.82365 EndZ=0
    g10: LineSegment StartX=-40.45 StartY=-8.82365 StartZ=0 EndX=-31.6263 EndY=0 EndZ=0
    g11: LineSegment StartX=-31.6263 StartY=0 StartZ=0 EndX=-40.45 EndY=8.82365 EndZ=0
    g12: LineSegment StartX=-40.45 StartY=8.82365 StartZ=0 EndX=-40.45 EndY=49.7763 EndZ=0
    g13: LineSegment StartX=-40.45 StartY=49.7763 StartZ=0 EndX=-20.4763 EndY=69.75 EndZ=0
    g14: LineSegment StartX=-7.19333e+06 StartY=68.6 StartZ=0 EndX=-7.19333e+06 EndY=69.75 EndZ=0
    g15: LineSegment StartX=-7.19333e+06 StartY=-68.6 StartZ=0 EndX=-7.19333e+06 EndY=-69.75 EndZ=0
    g16: LineSegment StartX=-40.45 StartY=-3.5966e+06 StartZ=0 EndX=-39.3 EndY=-3.5966e+06 EndZ=0
    g17: LineSegment StartX=-37.2391 StartY=5.61277 StartZ=0 EndX=-36.4259 EndY=6.42595 EndZ=0
    g18: LineSegment StartX=-39.3 StartY=10.8091 StartZ=0 EndX=-40.45 EndY=10.8091 EndZ=0
  constraints (55):
    c: Horizontal(g0)
    c: Coincident(g0,g1)
    c: Coincident(g1,g2)
    c: Vertical(g2)
    c: Coincident(g2,g3)
    c: PointOnObject(g3,g-1)
    c: Coincident(g3,g4)
    c: Coincident(g4,g5)
    c: Vertical(g5)
    c: Coincident(g5,g6)
    c: Coincident(g6,g7)
    c: Horizontal(g7)
    c: Coincident(g7,g8)
    c: Coincident(g8,g9)
    c: Vertical(g9)
    c: Coincident(g9,g10)
    c: Coincident(g10,g11)
    c: Coincident(g11,g12)
    c: Vertical(g12)
    c: Coincident(g12,g13)
    c: Coincident(g13,g0)
    c: Equal(g13,g1)
    c: Equal(g1,g6)
    c: Equal(g6,g8)
    c: Equal(g9,g5)
    c: Equal(g5,g7)
    c: Equal(g7,g0)
    c: Equal(g0,g2)
    c: Equal(g2,g12)
    c: Equal(g11,g3)
    c: Vertical(g11,g9)
    c: Vertical(g4,g2)
    c: Symmetric(g3,g10,g-2)
    c: Symmetric(g4,g9,g-2)
    c: Angle(g11) = 2.35619
    c: Equal(g11,g10)
    c: PointOnObject(g14,g-3)
    c: Vertical(g14)
    c: PointOnObject(g15,g-12)
    c: PointOnObject(g15,g7)
    c: Vertical(g15)
    c: Equal(g15,g14)
    c: PointOnObject(g16,g12)
    c: PointOnObject(g16,g-5)
    c: Horizontal(g16)
    c: Equal(g14,g16)
    c: Angle(g13) = 0.785398
    c: PointOnObject(g17,g11)
    c: PointOnObject(g17,g-6)
    c: PointOnObject(g18,g-5)
    c: PointOnObject(g18,g12)
    c: Horizontal(g18)
    c: Perpendicular(g-6,g17)
    c: Equal(g17,g18)
    c: DistanceX(g18,g18) = 1.15
FEATURE [PartDesign::Pad] Pad008
  Direction = (1,1,1)
  Length = 10
  Length2 = 100
  Profile = -> Sketch011
  Type = 0
FEATURE [PartDesign::Thickness] Thickness002
  Base = -> Pad008 [Face16]
  BaseFeature = -> Pad008
  Intersection = false
  Join = 0
  Mode = 0
  Reversed = true
  SupportTransform = false
  Value = 1
FEATURE [Sketcher::SketchObject] Sketch012
  ExternalGeometry = -> [ShapeBinder003]
  FullyConstrained = true
  MapMode = 5
  Placement = pos=(0,0,1) rot=(0,0,1;0rad)
  Support = -> [Thickness002]
  sketch-geometry (34):
    g0: LineSegment StartX=-29.3 StartY=48.8858 StartZ=0 EndX=-29.3 EndY=-48.8858 EndZ=0
    g1: LineSegment StartX=29.3 StartY=48.8858 StartZ=0 EndX=29.3 EndY=-48.8858 EndZ=0
    g2: LineSegment StartX=-19.5858 StartY=58.6 StartZ=0 EndX=19.5858 EndY=58.6 EndZ=0
    g3: LineSegment StartX=-19.5858 StartY=-58.6 StartZ=0 EndX=19.5858 EndY=-58.6 EndZ=0
    g4: LineSegment StartX=-16.5 StartY=63.6 StartZ=0 EndX=16.5 EndY=63.6 EndZ=0
    g5: LineSegment StartX=16.5 StartY=63.6 StartZ=0 EndX=16.5 EndY=53.6 EndZ=0
    g6: LineSegment StartX=16.5 StartY=53.6 StartZ=0 EndX=-16.5 EndY=53.6 EndZ=0
    g7: LineSegment StartX=-16.5 StartY=53.6 StartZ=0 EndX=-16.5 EndY=63.6 EndZ=0
    g8: LineSegment StartX=24.3 StartY=45.8 StartZ=0 EndX=34.3 EndY=45.8 EndZ=0
    g9: LineSegment StartX=34.3 StartY=45.8 StartZ=0 EndX=34.3 EndY=12.8 EndZ=0
    g10: LineSegment StartX=34.3 StartY=12.8 StartZ=0 EndX=24.3 EndY=12.8 EndZ=0
    g11: LineSegment StartX=24.3 StartY=12.8 StartZ=0 EndX=24.3 EndY=45.8 EndZ=0
    g12: LineSegment StartX=24.3 StartY=-12.8 StartZ=0 EndX=34.3 EndY=-12.8 EndZ=0
    g13: LineSegment StartX=34.3 StartY=-12.8 StartZ=0 EndX=34.3 EndY=-45.8 EndZ=0
    g14: LineSegment StartX=34.3 StartY=-45.8 StartZ=0 EndX=24.3 EndY=-45.8 EndZ=0
    g15: LineSegment StartX=24.3 StartY=-45.8 StartZ=0 EndX=24.3 EndY=-12.8 EndZ=0
    g16: LineSegment StartX=-34.3 StartY=-12.8 StartZ=0 EndX=-24.3 EndY=-12.8 EndZ=0
    g17: LineSegment StartX=-24.3 StartY=-12.8 StartZ=0 EndX=-24.3 EndY=-45.8 EndZ=0
    g18: LineSegment StartX=-24.3 StartY=-45.8 StartZ=0 EndX=-34.3 EndY=-45.8 EndZ=0
    g19: LineSegment StartX=-34.3 StartY=-45.8 StartZ=0 EndX=-34.3 EndY=-12.8 EndZ=0
    g20: LineSegment StartX=-16.5 StartY=-53.6 StartZ=0 EndX=16.5 EndY=-53.6 EndZ=0
    g21: LineSegment StartX=16.5 StartY=-53.6 StartZ=0 EndX=16.5 EndY=-63.6 EndZ=0
    g22: LineSegment StartX=16.5 StartY=-63.6 StartZ=0 EndX=-16.5 EndY=-63.6 EndZ=0
    g23: LineSegment StartX=-16.5 StartY=-63.6 StartZ=0 EndX=-16.5 EndY=-53.6 EndZ=0
    g24: LineSegment StartX=-34.3 StartY=45.8 StartZ=0 EndX=-24.3 EndY=45.8 EndZ=0
    g25: LineSegment StartX=-24.3 StartY=45.8 StartZ=0 EndX=-24.3 EndY=12.8 EndZ=0
    g26: LineSegment StartX=-24.3 StartY=12.8 StartZ=0 EndX=-34.3 EndY=12.8 EndZ=0
    g27: LineSegment StartX=-34.3 StartY=12.8 StartZ=0 EndX=-34.3 EndY=45.8 EndZ=0
    g28: LineSegment StartX=-16.5 StartY=5 StartZ=0 EndX=16.5 EndY=5 EndZ=0
    g29: LineSegment StartX=16.5 StartY=5 StartZ=0 EndX=16.5 EndY=-5 EndZ=0
    g30: LineSegment StartX=16.5 StartY=-5 StartZ=0 EndX=-16.5 EndY=-5 EndZ=0
    g31: LineSegment StartX=-16.5 StartY=-5 StartZ=0 EndX=-16.5 EndY=5 EndZ=0
    g32: LineSegment StartX=-38.3 StartY=-29.3 StartZ=0 EndX=38.3 EndY=-29.3 EndZ=0
    g33: LineSegment StartX=38.3 StartY=29.3 StartZ=0 EndX=-38.3 EndY=29.3 EndZ=0
  constraints (93):
    c: Symmetric(g-6,g-5,g0)
    c: Symmetric(g-4,g-3,g1)
    c: Horizontal(g1,g0)
    c: Horizontal(g0,g-6)
    c: Horizontal(g-14,g0)
    c: Horizontal(g0,g1)
    c: Horizontal(g2)
    c: Vertical(g3,g-16)
    c: Vertical(g3,g-15)
    c: Vertical(g-15,g2)
    c: Symmetric(g-15,g-16,g3)
    c: Symmetric(g-8,g-7,g2)
    c: Coincident(g4,g5)
    c: Coincident(g5,g6)
    c: Coincident(g6,g7)
    c: Coincident(g7,g4)
    c: Horizontal(g4)
    c: Horizontal(g6)
    c: Vertical(g7)
    c: Coincident(g8,g9)
    c: Coincident(g9,g10)
    c: Coincident(g10,g11)
    c: Coincident(g11,g8)
    c: Horizontal(g10)
    c: Vertical(g9)
    c: Coincident(g12,g13)
    c: Coincident(g13,g14)
    c: Coincident(g14,g15)
    c: Coincident(g15,g12)
    c: Horizontal(g12)
    c: Horizontal(g14)
    c: Vertical(g13)
    c: Vertical(g15)
    c: Coincident(g16,g17)
    c: Coincident(g17,g18)
    c: Coincident(g18,g19)
    c: Coincident(g19,g16)
    c: Horizontal(g16)
    c: Horizontal(g18)
    c: Vertical(g17)
    c: Coincident(g20,g21)
    c: Coincident(g21,g22)
    c: Coincident(g22,g23)
    c: Coincident(g23,g20)
    c: Horizontal(g22)
    c: Vertical(g21)
    c: DistanceX(g4,g4) = 33
    c: DistanceY(g7,g7) = 10
    c: Coincident(g24,g25)
    c: Coincident(g25,g26)
    c: Coincident(g26,g27)
    c: Coincident(g27,g24)
    c: Horizontal(g24)
    c: Vertical(g25)
    c: Vertical(g27)
    c: Equal(g6,g25)
    c: Equal(g25,g11)
    c: Equal(g11,g15)
    c: Equal(g15,g17)
    c: Equal(g17,g20)
    c: Equal(g7,g24)
    c: Equal(g24,g8)
    c: Equal(g8,g12)
    c: Equal(g12,g16)
    c: Equal(g16,g21)
    c: Coincident(g28,g29)
    c: Coincident(g29,g30)
    c: Coincident(g30,g31)
    c: Coincident(g31,g28)
    c: Horizontal(g30)
    c: Vertical(g29)
    c: Equal(g28,g4)
    c: Equal(g7,g31)
    c: Symmetric(g8,g8,g1)
    c: Vertical(g10,g12)
    c: Symmetric(g26,g25,g0)
    c: Vertical(g25,g16)
    c: Symmetric(g20,g22,g3)
    c: Symmetric(g20,g20,g-2)
    c: Vertical(g20,g5)
    c: Symmetric(g5,g4,g2)
    c: PointOnObject(g32,g-14)
    c: PointOnObject(g32,g-12)
    c: PointOnObject(g33,g-3)
    c: PointOnObject(g33,g-6)
    c: Symmetric(g-14,g-14,g32)
    c: Symmetric(g-6,g-6,g33)
    c: Symmetric(g8,g10,g33)
    c: Horizontal(g8,g24)
    c: Symmetric(g16,g18,g32)
    c: Horizontal(g16,g12)
    c: Symmetric(g28,g28,g-2)
    c: Symmetric(g30,g28,g-1)
FEATURE [PartDesign::Pad] Pad009
  BaseFeature = -> Thickness002
  Direction = (1,1,1)
  Length = 0.3
  Length2 = 100
  Profile = -> Sketch012
  Type = 0
FEATURE [Sketcher::SketchObject] Sketch013
  ExternalGeometry = -> [ShapeBinder003]
  FullyConstrained = true
  MapMode = 5
  Placement = pos=(0,0,1) rot=(0,0,1;0rad)
  Support = -> [Pad009]
  sketch-geometry (4):
    g0: Circle CenterX=-29.3 CenterY=6.71421 CenterZ=0 NormalX=0 NormalY=0 NormalZ=1 AngleXU=0 Radius=2.75
    g1: Circle CenterX=29.3 CenterY=-6.71421 CenterZ=0 NormalX=0 NormalY=0 NormalZ=1 AngleXU=0 Radius=2.75
    g2: Circle CenterX=0 CenterY=20 CenterZ=0 NormalX=0 NormalY=0 NormalZ=1 AngleXU=0 Radius=2.75
    g3: Circle CenterX=0 CenterY=-20 CenterZ=0 NormalX=0 NormalY=0 NormalZ=1 AngleXU=0 Radius=2.75
  constraints (11):
    c: Radius(g0) = 2.75
    c: Vertical(g0,g-4)
    c: Distance(g0,g-4) = 6
    c: Vertical(g1,g-6)
    c: Distance(g1,g-6) = 6
    c: Equal(g1,g0)
    c: PointOnObject(g2,g-2)
    c: Equal(g3,g2)
    c: Radius(g2) = 2.75
    c: Symmetric(g3,g2,g-1)
    c: DistanceY(g-1,g2) = 20
FEATURE [PartDesign::Pocket] Pocket003
  BaseFeature = -> Pad009
  Length = 5
  Length2 = 100
  Profile = -> Sketch013
  Type = 1
FEATURE [PartDesign::Body] Body025  label="back-regular"
  Group = -> [ShapeBinder003,Sketch011,Pad008,Thickness002,Sketch012,Pad009,Sketch013,Pocket003]
  Origin = -> Origin025
  Tip = -> Pocket003
FEATURE [PartDesign::FeatureBase] Clone006
  BaseFeature = -> Body008
FEATURE [PartDesign::Body] Body026
  BaseFeature = -> Body008
  Group = -> [Clone006]
  Origin = -> Origin026
  Placement = pos=(-49,0,0) rot=(0,0,1;0rad)
  Tip = -> Clone006
FEATURE [PartDesign::FeatureBase] Clone007
  BaseFeature = -> Body025
FEATURE [PartDesign::Body] Body027
  BaseFeature = -> Body025
  Group = -> [Clone007]
  Origin = -> Origin027
  Placement = pos=(49,0,0) rot=(0,0,1;0rad)
  Tip = -> Clone007
FEATURE [PartDesign::ShapeBinder] ShapeBinder004
  Placement = pos=(-49,0,0) rot=(0,0,1;0rad)
  Support = -> [Body026]
  TraceSupport = false
FEATURE [PartDesign::ShapeBinder] ShapeBinder005
  Placement = pos=(49,0,0) rot=(0,0,1;0rad)
  Support = -> [Body027]
  TraceSupport = false
FEATURE [Sketcher::SketchObject] Sketch014
  ExternalGeometry = -> [ShapeBinder004,ShapeBinder005]
  FullyConstrained = true
  MapMode = 5
  Support = -> [XY_Plane028]
  sketch-geometry (14):
    g0: LineSegment StartX=8.55 StartY=49.7763 StartZ=0 EndX=8.55 EndY=8.82365 EndZ=0
    g1: LineSegment StartX=8.55 StartY=8.82365 StartZ=0 EndX=17.3737 EndY=0 EndZ=0
    g2: LineSegment StartX=17.3737 StartY=0 StartZ=0 EndX=8.55 EndY=-8.82365 EndZ=0
    g3: LineSegment StartX=8.55 StartY=-8.82365 StartZ=0 EndX=8.55 EndY=-49.7763 EndZ=0
    g4: LineSegment StartX=-8.55 StartY=-49.7763 StartZ=0 EndX=-8.55 EndY=-8.82365 EndZ=0
    g5: LineSegment StartX=-8.55 StartY=-8.82365 StartZ=0 EndX=-17.3737 EndY=0 EndZ=0
    g6: LineSegment StartX=-17.3737 StartY=0 StartZ=0 EndX=-8.55 EndY=8.82365 EndZ=0
    g7: LineSegment StartX=-8.55 StartY=8.82365 StartZ=0 EndX=-8.55 EndY=49.7763 EndZ=0
    g8: LineSegment StartX=8.55 StartY=49.7763 StartZ=0 EndX=28.5237 EndY=69.75 EndZ=0
    g9: LineSegment StartX=28.5237 StartY=69.75 StartZ=0 EndX=-28.5237 EndY=69.75 EndZ=0
    g10: LineSegment StartX=-28.5237 StartY=69.75 StartZ=0 EndX=-8.55 EndY=49.7763 EndZ=0
    g11: LineSegment StartX=-8.55 StartY=-49.7763 StartZ=0 EndX=-28.5237 EndY=-69.75 EndZ=0
    g12: LineSegment StartX=-28.5237 StartY=-69.75 StartZ=0 EndX=28.5237 EndY=-69.75 EndZ=0
    g13: LineSegment StartX=28.5237 StartY=-69.75 StartZ=0 EndX=8.55 EndY=-49.7763 EndZ=0
  constraints (28):
    c: Coincident(g0,g1)
    c: Coincident(g1,g2)
    c: Coincident(g2,g3)
    c: Coincident(g4,g5)
    c: Coincident(g5,g6)
    c: Coincident(g6,g7)
    c: Coincident(g0,g-8)
    c: Coincident(g1,g-11)
    c: Coincident(g2,g-11)
    c: Coincident(g3,g-10)
    c: Coincident(g4,g-12)
    c: Coincident(g5,g-12)
    c: Coincident(g6,g-6)
    c: Coincident(g0,g8)
    c: Coincident(g8,g-15)
    c: Coincident(g8,g9)
    c: Coincident(g9,g-16)
    c: Coincident(g9,g10)
    c: Coincident(g10,g7)
    c: Coincident(g4,g11)
    c: Coincident(g11,g-13)
    c: Coincident(g11,g12)
    c: Coincident(g12,g-14)
    c: Coincident(g12,g13)
    c: Coincident(g13,g3)
    c: Coincident(g-13,g4)
    c: Coincident(g0,g-15)
    c: Coincident(g7,g-16)
FEATURE [PartDesign::Pad] Pad010
  Direction = (1,1,1)
  Length = 2
  Length2 = 100
  Profile = -> Sketch014
  Type = 0
FEATURE [PartDesign::Body] Body028
  Group = -> [ShapeBinder004,ShapeBinder005,Sketch014,Pad010]
  Origin = -> Origin028
  Tip = -> Pad010
FEATURE [Part::MultiFuse] Fusion001  label="panel-left"
  Placement = pos=(-112,0,0) rot=(0,0,1;0rad)
  Shapes = -> [Body026,Body027,Body028]
FEATURE [PartDesign::FeatureBase] Clone008
  BaseFeature = -> Body025
FEATURE [PartDesign::Body] Body029
  BaseFeature = -> Body025
  Group = -> [Clone008]
  Origin = -> Origin029
  Placement = pos=(-49,0,0) rot=(0,0,1;0rad)
  Tip = -> Clone008
FEATURE [PartDesign::FeatureBase] Clone010
  BaseFeature = -> Body028
FEATURE [PartDesign::Body] Body031
  BaseFeature = -> Body028
  Group = -> [Clone010]
  Origin = -> Origin031
  Tip = -> Clone010
FEATURE [PartDesign::ShapeBinder] ShapeBinder006
  Placement = pos=(-112,0,0) rot=(0,0,1;0rad)
  Support = -> [Fusion001]
  TraceSupport = false
FEATURE [PartDesign::ShapeBinder] ShapeBinder019
  Support = -> [Fusion]
  TraceSupport = false
FEATURE [Sketcher::SketchObject] Sketch039
  ExternalGeometry = -> [ShapeBinder019]
  FullyConstrained = false
  MapMode = 5
  Support = -> [XY_Plane049]
  sketch-geometry (19):
    g0: LineSegment StartX=-20.4763 StartY=69.75 StartZ=0 EndX=20.4763 EndY=69.75 EndZ=0
    g1: LineSegment StartX=20.4763 StartY=69.75 StartZ=0 EndX=40.45 EndY=49.7763 EndZ=0
    g2: LineSegment StartX=40.45 StartY=49.7763 StartZ=0 EndX=40.45 EndY=8.82365 EndZ=0
    g3: LineSegment StartX=40.45 StartY=8.82365 StartZ=0 EndX=31.6263 EndY=0 EndZ=0
    g4: LineSegment StartX=31.6263 StartY=0 StartZ=0 EndX=40.45 EndY=-8.82365 EndZ=0
    g5: LineSegment StartX=40.45 StartY=-8.82365 StartZ=0 EndX=40.45 EndY=-49.7763 EndZ=0
    g6: LineSegment StartX=40.45 StartY=-49.7763 StartZ=0 EndX=20.4763 EndY=-69.75 EndZ=0
    g7: LineSegment StartX=20.4763 StartY=-69.75 StartZ=0 EndX=-20.4763 EndY=-69.75 EndZ=0
    g8: LineSegment StartX=-20.4763 StartY=-69.75 StartZ=0 EndX=-40.45 EndY=-49.7763 EndZ=0
    g9: LineSegment StartX=-40.45 StartY=-49.7763 StartZ=0 EndX=-40.45 EndY=-8.82365 EndZ=0
    g10: LineSegment StartX=-40.45 StartY=-8.82365 StartZ=0 EndX=-31.6263 EndY=0 EndZ=0
    g11: LineSegment StartX=-31.6263 StartY=0 StartZ=0 EndX=-40.45 EndY=8.82365 EndZ=0
    g12: LineSegment StartX=-40.45 StartY=8.82365 StartZ=0 EndX=-40.45 EndY=49.7763 EndZ=0
    g13: LineSegment StartX=-40.45 StartY=49.7763 StartZ=0 EndX=-20.4763 EndY=69.75 EndZ=0
    g14: LineSegment StartX=-7.19333e+06 StartY=68.6 StartZ=0 EndX=-7.19333e+06 EndY=69.75 EndZ=0
    g15: LineSegment StartX=-7.19333e+06 StartY=-68.6 StartZ=0 EndX=-7.19333e+06 EndY=-69.75 EndZ=0
    g16: LineSegment StartX=-40.45 StartY=-3.5966e+06 StartZ=0 EndX=-39.3 EndY=-3.5966e+06 EndZ=0
    g17: LineSegment StartX=-37.2391 StartY=5.61277 StartZ=0 EndX=-36.4259 EndY=6.42595 EndZ=0
    g18: LineSegment StartX=-39.3 StartY=10.8091 StartZ=0 EndX=-40.45 EndY=10.8091 EndZ=0
  constraints (55):
    c: Horizontal(g0)
    c: Coincident(g0,g1)
    c: Coincident(g1,g2)
    c: Vertical(g2)
    c: Coincident(g2,g3)
    c: PointOnObject(g3,g-1)
    c: Coincident(g3,g4)
    c: Coincident(g4,g5)
    c: Vertical(g5)
    c: Coincident(g5,g6)
    c: Coincident(g6,g7)
    c: Horizontal(g7)
    c: Coincident(g7,g8)
    c: Coincident(g8,g9)
    c: Vertical(g9)
    c: Coincident(g9,g10)
    c: Coincident(g10,g11)
    c: Coincident(g11,g12)
    c: Vertical(g12)
    c: Coincident(g12,g13)
    c: Coincident(g13,g0)
    c: Equal(g13,g1)
    c: Equal(g1,g6)
    c: Equal(g6,g8)
    c: Equal(g9,g5)
    c: Equal(g5,g7)
    c: Equal(g7,g0)
    c: Equal(g0,g2)
    c: Equal(g2,g12)
    c: Equal(g11,g3)
    c: Vertical(g11,g9)
    c: Vertical(g4,g2)
    c: Symmetric(g3,g10,g-2)
    c: Symmetric(g4,g9,g-2)
    c: Angle(g11) = 2.35619
    c: Equal(g11,g10)
    c: PointOnObject(g14,g-3)
    c: Vertical(g14)
    c: PointOnObject(g15,g-12)
    c: PointOnObject(g15,g7)
    c: Vertical(g15)
    c: Equal(g15,g14)
    c: PointOnObject(g16,g12)
    c: PointOnObject(g16,g-5)
    c: Horizontal(g16)
    c: Equal(g14,g16)
    c: Angle(g13) = 0.785398
    c: PointOnObject(g17,g11)
    c: PointOnObject(g17,g-6)
    c: PointOnObject(g18,g-5)
    c: PointOnObject(g18,g12)
    c: Horizontal(g18)
    c: Perpendicular(g-6,g17)
    c: Equal(g17,g18)
    c: DistanceX(g18,g18) = 1.15
FEATURE [PartDesign::Pad] Pad026
  Direction = (1,1,1)
  Length = 10
  Length2 = 100
  Profile = -> Sketch039
  Type = 0
FEATURE [PartDesign::Thickness] Thickness004
  Base = -> Pad026 [Face16]
  BaseFeature = -> Pad026
  Intersection = false
  Join = 0
  Mode = 0
  Reversed = true
  SupportTransform = false
  Value = 1
FEATURE [Sketcher::SketchObject] Sketch040
  ExternalGeometry = -> [ShapeBinder019]
  FullyConstrained = true
  MapMode = 5
  Placement = pos=(0,0,1) rot=(0,0,1;0rad)
  Support = -> [Thickness004]
  sketch-geometry (34):
    g0: LineSegment StartX=-29.3 StartY=48.8858 StartZ=0 EndX=-29.3 EndY=-48.8858 EndZ=0
    g1: LineSegment StartX=29.3 StartY=48.8858 StartZ=0 EndX=29.3 EndY=-48.8858 EndZ=0
    g2: LineSegment StartX=-19.5858 StartY=58.6 StartZ=0 EndX=19.5858 EndY=58.6 EndZ=0
    g3: LineSegment StartX=-19.5858 StartY=-58.6 StartZ=0 EndX=19.5858 EndY=-58.6 EndZ=0
    g4: LineSegment StartX=-16.5 StartY=63.6 StartZ=0 EndX=16.5 EndY=63.6 EndZ=0
    g5: LineSegment StartX=16.5 StartY=63.6 StartZ=0 EndX=16.5 EndY=53.6 EndZ=0
    g6: LineSegment StartX=16.5 StartY=53.6 StartZ=0 EndX=-16.5 EndY=53.6 EndZ=0
    g7: LineSegment StartX=-16.5 StartY=53.6 StartZ=0 EndX=-16.5 EndY=63.6 EndZ=0
    g8: LineSegment StartX=24.3 StartY=45.8 StartZ=0 EndX=34.3 EndY=45.8 EndZ=0
    g9: LineSegment StartX=34.3 StartY=45.8 StartZ=0 EndX=34.3 EndY=12.8 EndZ=0
    g10: LineSegment StartX=34.3 StartY=12.8 StartZ=0 EndX=24.3 EndY=12.8 EndZ=0
    g11: LineSegment StartX=24.3 StartY=12.8 StartZ=0 EndX=24.3 EndY=45.8 EndZ=0
    g12: LineSegment StartX=24.3 StartY=-12.8 StartZ=0 EndX=34.3 EndY=-12.8 EndZ=0
    g13: LineSegment StartX=34.3 StartY=-12.8 StartZ=0 EndX=34.3 EndY=-45.8 EndZ=0
    g14: LineSegment StartX=34.3 StartY=-45.8 StartZ=0 EndX=24.3 EndY=-45.8 EndZ=0
    g15: LineSegment StartX=24.3 StartY=-45.8 StartZ=0 EndX=24.3 EndY=-12.8 EndZ=0
    g16: LineSegment StartX=-34.3 StartY=-12.8 StartZ=0 EndX=-24.3 EndY=-12.8 EndZ=0
    g17: LineSegment StartX=-24.3 StartY=-12.8 StartZ=0 EndX=-24.3 EndY=-45.8 EndZ=0
    g18: LineSegment StartX=-24.3 StartY=-45.8 StartZ=0 EndX=-34.3 EndY=-45.8 EndZ=0
    g19: LineSegment StartX=-34.3 StartY=-45.8 StartZ=0 EndX=-34.3 EndY=-12.8 EndZ=0
    g20: LineSegment StartX=-16.5 StartY=-53.6 StartZ=0 EndX=16.5 EndY=-53.6 EndZ=0
    g21: LineSegment StartX=16.5 StartY=-53.6 StartZ=0 EndX=16.5 EndY=-63.6 EndZ=0
    g22: LineSegment StartX=16.5 StartY=-63.6 StartZ=0 EndX=-16.5 EndY=-63.6 EndZ=0
    g23: LineSegment StartX=-16.5 StartY=-63.6 StartZ=0 EndX=-16.5 EndY=-53.6 EndZ=0
    g24: LineSegment StartX=-34.3 StartY=45.8 StartZ=0 EndX=-24.3 EndY=45.8 EndZ=0
    g25: LineSegment StartX=-24.3 StartY=45.8 StartZ=0 EndX=-24.3 EndY=12.8 EndZ=0
    g26: LineSegment StartX=-24.3 StartY=12.8 StartZ=0 EndX=-34.3 EndY=12.8 EndZ=0
    g27: LineSegment StartX=-34.3 StartY=12.8 StartZ=0 EndX=-34.3 EndY=45.8 EndZ=0
    g28: LineSegment StartX=-16.5 StartY=5 StartZ=0 EndX=16.5 EndY=5 EndZ=0
    g29: LineSegment StartX=16.5 StartY=5 StartZ=0 EndX=16.5 EndY=-5 EndZ=0
    g30: LineSegment StartX=16.5 StartY=-5 StartZ=0 EndX=-16.5 EndY=-5 EndZ=0
    g31: LineSegment StartX=-16.5 StartY=-5 StartZ=0 EndX=-16.5 EndY=5 EndZ=0
    g32: LineSegment StartX=-38.3 StartY=-29.3 StartZ=0 EndX=38.3 EndY=-29.3 EndZ=0
    g33: LineSegment StartX=38.3 StartY=29.3 StartZ=0 EndX=-38.3 EndY=29.3 EndZ=0
  constraints (93):
    c: Symmetric(g-6,g-5,g0)
    c: Symmetric(g-4,g-3,g1)
    c: Horizontal(g1,g0)
    c: Horizontal(g0,g-6)
    c: Horizontal(g-14,g0)
    c: Horizontal(g0,g1)
    c: Horizontal(g2)
    c: Vertical(g3,g-16)
    c: Vertical(g3,g-15)
    c: Vertical(g-15,g2)
    c: Symmetric(g-15,g-16,g3)
    c: Symmetric(g-8,g-7,g2)
    c: Coincident(g4,g5)
    c: Coincident(g5,g6)
    c: Coincident(g6,g7)
    c: Coincident(g7,g4)
    c: Horizontal(g4)
    c: Horizontal(g6)
    c: Vertical(g7)
    c: Coincident(g8,g9)
    c: Coincident(g9,g10)
    c: Coincident(g10,g11)
    c: Coincident(g11,g8)
    c: Horizontal(g10)
    c: Vertical(g9)
    c: Coincident(g12,g13)
    c: Coincident(g13,g14)
    c: Coincident(g14,g15)
    c: Coincident(g15,g12)
    c: Horizontal(g12)
    c: Horizontal(g14)
    c: Vertical(g13)
    c: Vertical(g15)
    c: Coincident(g16,g17)
    c: Coincident(g17,g18)
    c: Coincident(g18,g19)
    c: Coincident(g19,g16)
    c: Horizontal(g16)
    c: Horizontal(g18)
    c: Vertical(g17)
    c: Coincident(g20,g21)
    c: Coincident(g21,g22)
    c: Coincident(g22,g23)
    c: Coincident(g23,g20)
    c: Horizontal(g22)
    c: Vertical(g21)
    c: DistanceX(g4,g4) = 33
    c: DistanceY(g7,g7) = 10
    c: Coincident(g24,g25)
    c: Coincident(g25,g26)
    c: Coincident(g26,g27)
    c: Coincident(g27,g24)
    c: Horizontal(g24)
    c: Vertical(g25)
    c: Vertical(g27)
    c: Equal(g6,g25)
    c: Equal(g25,g11)
    c: Equal(g11,g15)
    c: Equal(g15,g17)
    c: Equal(g17,g20)
    c: Equal(g7,g24)
    c: Equal(g24,g8)
    c: Equal(g8,g12)
    c: Equal(g12,g16)
    c: Equal(g16,g21)
    c: Coincident(g28,g29)
    c: Coincident(g29,g30)
    c: Coincident(g30,g31)
    c: Coincident(g31,g28)
    c: Horizontal(g30)
    c: Vertical(g29)
    c: Equal(g28,g4)
    c: Equal(g7,g31)
    c: Symmetric(g8,g8,g1)
    c: Vertical(g10,g12)
    c: Symmetric(g26,g25,g0)
    c: Vertical(g25,g16)
    c: Symmetric(g20,g22,g3)
    c: Symmetric(g20,g20,g-2)
    c: Vertical(g20,g5)
    c: Symmetric(g5,g4,g2)
    c: PointOnObject(g32,g-14)
    c: PointOnObject(g32,g-12)
    c: PointOnObject(g33,g-3)
    c: PointOnObject(g33,g-6)
    c: Symmetric(g-14,g-14,g32)
    c: Symmetric(g-6,g-6,g33)
    c: Symmetric(g8,g10,g33)
    c: Horizontal(g8,g24)
    c: Symmetric(g16,g18,g32)
    c: Horizontal(g16,g12)
    c: Symmetric(g28,g28,g-2)
    c: Symmetric(g30,g28,g-1)
FEATURE [PartDesign::Pad] Pad027
  BaseFeature = -> Thickness004
  Direction = (1,1,1)
  Length = 0.3
  Length2 = 100
  Profile = -> Sketch040
  Type = 0
FEATURE [Sketcher::SketchObject] Sketch038
  ExternalGeometry = -> [ShapeBinder019]
  FullyConstrained = true
  MapMode = 5
  Placement = pos=(0,0,1) rot=(0,0,1;0rad)
  Support = -> [Pad027]
  sketch-geometry (1):
    g0: Circle CenterX=-29.3 CenterY=6.71421 CenterZ=0 NormalX=0 NormalY=0 NormalZ=1 AngleXU=0 Radius=2.75
  constraints (3):
    c: Radius(g0) = 2.75
    c: Vertical(g0,g-4)
    c: Distance(g0,g-4) = 6
FEATURE [PartDesign::Pocket] Pocket011
  BaseFeature = -> Pad027
  Length = 5
  Length2 = 100
  Profile = -> Sketch038
  Type = 1
FEATURE [PartDesign::Body] Body048  label="back-regular-last"
  Group = -> [ShapeBinder019,Sketch039,Pad026,Thickness004,Sketch040,Pad027,Sketch038,Pocket011]
  Origin = -> Origin048
  Tip = -> Pocket011
FEATURE [PartDesign::FeatureBase] Clone011
  BaseFeature = -> Body048
FEATURE [PartDesign::Body] Body049
  Group = -> [Clone011]
  Origin = -> Origin049
  Placement = pos=(49,0,0) rot=(0,0,1;0rad)
  Tip = -> Clone011
FEATURE [Part::MultiFuse] Fusion002  label="panel-right"
  Placement = pos=(112,0,0) rot=(0,0,1;0rad)
  Shapes = -> [Body029,Body031,Body049]
FEATURE [PartDesign::ShapeBinder] ShapeBinder007
  Placement = pos=(112,0,0) rot=(0,0,1;0rad)
  Support = -> [Fusion002]
  TraceSupport = false
FEATURE [Sketcher::SketchObject] Sketch015
  ExternalGeometry = -> [ShapeBinder006,ShapeBinder007]
  FullyConstrained = true
  MapMode = 5
  Support = -> [XY_Plane032]
  sketch-geometry (10):
    g0: LineSegment StartX=-22.55 StartY=-8.82365 StartZ=0 EndX=-31.3737 EndY=0 EndZ=0
    g1: LineSegment StartX=-31.3737 StartY=0 StartZ=0 EndX=-22.55 EndY=8.82365 EndZ=0
    g2: LineSegment StartX=-22.55 StartY=8.82365 StartZ=0 EndX=-22.55 EndY=49.7763 EndZ=0
    g3: LineSegment StartX=22.55 StartY=-49.7763 StartZ=0 EndX=22.55 EndY=-8.82365 EndZ=0
    g4: LineSegment StartX=22.55 StartY=-8.82365 StartZ=0 EndX=31.3737 EndY=0 EndZ=0
    g5: LineSegment StartX=31.3737 StartY=0 StartZ=0 EndX=22.55 EndY=8.82365 EndZ=0
    g6: LineSegment StartX=22.55 StartY=8.82365 StartZ=0 EndX=22.55 EndY=49.7763 EndZ=0
    g7: LineSegment StartX=22.55 StartY=49.7763 StartZ=0 EndX=-22.55 EndY=49.7763 EndZ=0
    g8: LineSegment StartX=-22.55 StartY=-8.82365 StartZ=0 EndX=-22.55 EndY=-49.7763 EndZ=0
    g9: LineSegment StartX=22.55 StartY=-49.7763 StartZ=0 EndX=-22.55 EndY=-49.7763 EndZ=0
  constraints (20):
    c: Coincident(g0,g-6)
    c: Coincident(g0,g1)
    c: Coincident(g1,g2)
    c: Coincident(g1,g-6)
    c: Coincident(g3,g-11)
    c: Coincident(g3,g4)
    c: Coincident(g4,g-11)
    c: Coincident(g4,g5)
    c: Coincident(g5,g-10)
    c: Coincident(g5,g6)
    c: Coincident(g6,g-7)
    c: Coincident(g6,g7)
    c: Coincident(g7,g2)
    c: Coincident(g2,g-3)
    c: Coincident(g0,g-5)
    c: Coincident(g8,g0)
    c: Coincident(g8,g-4)
    c: Coincident(g3,g-8)
    c: Coincident(g9,g3)
    c: Coincident(g9,g8)
FEATURE [PartDesign::Pad] Pad011
  Direction = (1,1,1)
  Length = 10
  Length2 = 100
  Profile = -> Sketch015
  Type = 0
FEATURE [PartDesign::Thickness] Thickness003
  Base = -> Pad011 [Face12]
  BaseFeature = -> Pad011
  Intersection = false
  Join = 0
  Mode = 0
  Reversed = true
  SupportTransform = false
  Value = 1
FEATURE [Sketcher::SketchObject] Sketch016
  FullyConstrained = true
  MapMode = 5
  Placement = pos=(0,0,1) rot=(0,0,1;0rad)
  Support = -> [Thickness003]
  sketch-geometry (4):
    g0: LineSegment StartX=-5 StartY=26 StartZ=0 EndX=5 EndY=26 EndZ=0
    g1: LineSegment StartX=5 StartY=26 StartZ=0 EndX=5 EndY=10 EndZ=0
    g2: LineSegment StartX=5 StartY=10 StartZ=0 EndX=-5 EndY=10 EndZ=0
    g3: LineSegment StartX=-5 StartY=10 StartZ=0 EndX=-5 EndY=26 EndZ=0
  constraints (11):
    c: Coincident(g0,g1)
    c: Coincident(g1,g2)
    c: Coincident(g2,g3)
    c: Coincident(g3,g0)
    c: Horizontal(g2)
    c: Vertical(g1)
    c: Vertical(g3)
    c: DistanceY(g-1,g2) = 10
    c: DistanceX(g0,g0) = 10
    c: DistanceY(g3,g3) = 16
    c: Symmetric(g0,g0,g-2)
FEATURE [PartDesign::Pad] Pad012
  BaseFeature = -> Thickness003
  Direction = (1,1,1)
  Length = 0.3
  Length2 = 100
  Profile = -> Sketch016
  Type = 0
FEATURE [PartDesign::Mirrored] Mirrored
  BaseFeature = -> Pad012
  MirrorPlane = -> Sketch016 [H_Axis]
  Originals = -> [Pad012]
FEATURE [Sketcher::SketchObject] Sketch017
  ExternalGeometry = -> [ShapeBinder006]
  FullyConstrained = true
  MapMode = 5
  Placement = pos=(0,0,1) rot=(0,0,1;0rad)
  Support = -> [Mirrored]
  sketch-geometry (1):
    g0: Circle CenterX=-21.3737 CenterY=0 CenterZ=0 NormalX=0 NormalY=0 NormalZ=1 AngleXU=0 Radius=2.75
  constraints (3):
    c: PointOnObject(g0,g-1)
    c: Radius(g0) = 2.75
    c: DistanceX(g-4,g0) = 10
FEATURE [PartDesign::Pocket] Pocket004
  BaseFeature = -> Mirrored
  Length = 5
  Length2 = 100
  Profile = -> Sketch017
  Type = 0
FEATURE [PartDesign::Mirrored] Mirrored001
  BaseFeature = -> Pocket004
  MirrorPlane = -> Sketch017 [V_Axis]
  Originals = -> [Pocket004]
FEATURE [PartDesign::Body] Body032  label="panel-center"
  Group = -> [ShapeBinder006,ShapeBinder007,Sketch015,Pad011,Thickness003,Sketch016,Pad012,Mirrored,Sketch017,Pocket004,Mirrored001]
  Origin = -> Origin032
  Tip = -> Mirrored001
FEATURE [Part::MultiFuse] Fusion003  label="board"
  Shapes = -> [Body032,Fusion001,Fusion002]
FEATURE [PartDesign::ShapeBinder] ShapeBinder008
  Support = -> [Fusion003]
  TraceSupport = false
FEATURE [Sketcher::SketchObject] Sketch018
  ExternalGeometry = -> [ShapeBinder008]
  FullyConstrained = true
  MapMode = 5
  Support = -> [XY_Plane033]
  sketch-geometry (5):
    g0: LineSegment StartX=-70 StartY=15 StartZ=0 EndX=70 EndY=15 EndZ=0
    g1: LineSegment StartX=70 StartY=15 StartZ=0 EndX=70 EndY=25 EndZ=0
    g2: LineSegment StartX=70 StartY=25 StartZ=0 EndX=-70 EndY=25 EndZ=0
    g3: LineSegment StartX=-70 StartY=25 StartZ=0 EndX=-70 EndY=15 EndZ=0
    g4: LineSegment StartX=63 StartY=20 StartZ=0 EndX=-63 EndY=20 EndZ=0
  constraints (12):
    c: Coincident(g0,g1)
    c: Coincident(g1,g2)
    c: Coincident(g2,g3)
    c: Coincident(g3,g0)
    c: Horizontal(g2)
    c: Vertical(g1)
    c: Symmetric(g0,g0,g-2)
    c: Symmetric(g2,g0,g4)
    c: DistanceY(g1,g1) = 10
    c: Coincident(g4,g-4)
    c: Coincident(g4,g-3)
    c: DistanceX(g2,g2) = 140
FEATURE [PartDesign::Pad] Pad013
  Direction = (1,1,1)
  Length = 2
  Length2 = 100
  Profile = -> Sketch018
  Reversed = true
  Type = 0
FEATURE [PartDesign::ShapeBinder] ShapeBinder009
  Support = -> [Body032]
  TraceSupport = false
FEATURE [Sketcher::SketchObject] Sketch019
  ExternalGeometry = -> [ShapeBinder009]
  FullyConstrained = true
  MapMode = 5
  Support = -> [XY_Plane034]
  sketch-geometry (10):
    g0: LineSegment StartX=-22.55 StartY=49.7763 StartZ=0 EndX=22.55 EndY=49.7763 EndZ=0
    g1: LineSegment StartX=22.55 StartY=49.7763 StartZ=0 EndX=22.55 EndY=8.82365 EndZ=0
    g2: LineSegment StartX=22.55 StartY=8.82365 StartZ=0 EndX=31.3737 EndY=0 EndZ=0
    g3: LineSegment StartX=31.3737 StartY=0 StartZ=0 EndX=22.55 EndY=-8.82365 EndZ=0
    g4: LineSegment StartX=22.55 StartY=-8.82365 StartZ=0 EndX=22.55 EndY=-49.7763 EndZ=0
    g5: LineSegment StartX=22.55 StartY=-49.7763 StartZ=0 EndX=-22.55 EndY=-49.7763 EndZ=0
    g6: LineSegment StartX=-22.55 StartY=-49.7763 StartZ=0 EndX=-22.55 EndY=-8.82365 EndZ=0
    g7: LineSegment StartX=-22.55 StartY=-8.82365 StartZ=0 EndX=-31.3737 EndY=0 EndZ=0
    g8: LineSegment StartX=-31.3737 StartY=0 StartZ=0 EndX=-22.55 EndY=8.82365 EndZ=0
    g9: LineSegment StartX=-22.55 StartY=8.82365 StartZ=0 EndX=-22.55 EndY=49.7763 EndZ=0
  constraints (20):
    c: Coincident(g-11,g0)
    c: Coincident(g0,g-11)
    c: Coincident(g0,g1)
    c: Coincident(g1,g-9)
    c: Coincident(g1,g2)
    c: Coincident(g2,g-8)
    c: Coincident(g2,g3)
    c: Coincident(g3,g-7)
    c: Coincident(g3,g4)
    c: Coincident(g4,g-6)
    c: Coincident(g4,g5)
    c: Coincident(g5,g-5)
    c: Coincident(g5,g6)
    c: Coincident(g6,g-4)
    c: Coincident(g6,g7)
    c: Coincident(g7,g-12)
    c: Coincident(g7,g8)
    c: Coincident(g8,g-12)
    c: Coincident(g8,g9)
    c: Coincident(g9,g0)
FEATURE [PartDesign::Pad] Pad014
  Direction = (1,1,1)
  Length = 1
  Length2 = 100
  Profile = -> Sketch019
  Type = 0
FEATURE [Sketcher::SketchObject] Sketch020
  ExternalGeometry = -> [Pad014]
  FullyConstrained = true
  MapMode = 5
  Placement = pos=(0,0,0) rot=(1,0,0;3.14159rad)
  Support = -> [Pad014]
  sketch-geometry (8):
    g0: LineSegment StartX=-22.55 StartY=49.7763 StartZ=0 EndX=22.55 EndY=49.7763 EndZ=0
    g1: LineSegment StartX=22.55 StartY=49.7763 StartZ=0 EndX=22.55 EndY=48.7763 EndZ=0
    g2: LineSegment StartX=22.55 StartY=48.7763 StartZ=0 EndX=-22.55 EndY=48.7763 EndZ=0
    g3: LineSegment StartX=-22.55 StartY=48.7763 StartZ=0 EndX=-22.55 EndY=49.7763 EndZ=0
    g4: LineSegment StartX=-22.55 StartY=-49.7763 StartZ=0 EndX=22.55 EndY=-49.7763 EndZ=0
    g5: LineSegment StartX=22.55 StartY=-49.7763 StartZ=0 EndX=22.55 EndY=-48.7763 EndZ=0
    g6: LineSegment StartX=22.55 StartY=-48.7763 StartZ=0 EndX=-22.55 EndY=-48.7763 EndZ=0
    g7: LineSegment StartX=-22.55 StartY=-48.7763 StartZ=0 EndX=-22.55 EndY=-49.7763 EndZ=0
  constraints (20):
    c: Coincident(g0,g1)
    c: Coincident(g1,g2)
    c: Coincident(g2,g3)
    c: Coincident(g3,g0)
    c: Horizontal(g2)
    c: Vertical(g1)
    c: Vertical(g3)
    c: Coincident(g0,g-3)
    c: Coincident(g4,g5)
    c: Coincident(g5,g6)
    c: Coincident(g6,g7)
    c: Coincident(g7,g4)
    c: Horizontal(g6)
    c: Vertical(g5)
    c: Vertical(g7)
    c: Coincident(g4,g-4)
    c: Coincident(g4,g-4)
    c: Coincident(g0,g-3)
    c: Equal(g3,g7)
    c: DistanceY(g3,g3) = 1
FEATURE [PartDesign::Pad] Pad015
  BaseFeature = -> Pad014
  Direction = (1,1,1)
  Length = 10
  Length2 = 100
  Profile = -> Sketch020
  Type = 0
FEATURE [Sketcher::SketchObject] Sketch021
  ExternalGeometry = -> [ShapeBinder009]
  FullyConstrained = true
  MapMode = 5
  Placement = pos=(0,0,1) rot=(0,0,1;0rad)
  Support = -> [Pad015]
  sketch-geometry (2):
    g0: Circle CenterX=0 CenterY=18 CenterZ=0 NormalX=0 NormalY=0 NormalZ=1 AngleXU=0 Radius=11.4
    g1: LineSegment StartX=5 StartY=18 StartZ=0 EndX=-5 EndY=18 EndZ=0
  constraints (6):
    c: PointOnObject(g0,g-2)
    c: PointOnObject(g1,g-4)
    c: PointOnObject(g1,g-3)
    c: Symmetric(g-4,g-4,g1)
    c: PointOnObject(g0,g1)
    c: Radius(g0) = 11.4
FEATURE [PartDesign::Pocket] Pocket005
  BaseFeature = -> Pad015
  Length = 5
  Length2 = 100
  Profile = -> Sketch021
  Type = 0
FEATURE [PartDesign::Mirrored] Mirrored002
  BaseFeature = -> Pocket005
  MirrorPlane = -> Sketch021 [H_Axis]
  Originals = -> [Pocket005]
FEATURE [PartDesign::Body] Body034  label="panel-center-top"
  Group = -> [ShapeBinder009,Sketch019,Pad014,Sketch020,Pad015,Sketch021,Pocket005,Mirrored002]
  Origin = -> Origin034
  Placement = pos=(0,0,10) rot=(0,0,1;0rad)
  Tip = -> Mirrored002
FEATURE [Sketcher::SketchObject] Sketch026
  ExternalGeometry = -> [ShapeBinder008]
  FullyConstrained = false
  MapMode = 5
  Support = -> [Pad013]
  sketch-geometry (2):
    g0: Circle CenterX=-62.9953 CenterY=20.0064 CenterZ=0 NormalX=0 NormalY=0 NormalZ=1 AngleXU=0 Radius=2.54206
    g1: LineSegment StartX=-61.5439 StartY=22.0934 StartZ=0 EndX=-61.4297 EndY=22.2576 EndZ=0
  constraints (4):
    c: PointOnObject(g1,g0)
    c: PointOnObject(g1,g-3)
    c: Perpendicular(g-3,g1)
    c: Distance(g1) = 0.2
FEATURE [PartDesign::Pad] Pad018
  BaseFeature = -> Pad013
  Direction = (1,1,1)
  Length = 1
  Length2 = 100
  Profile = -> Sketch026
  Type = 0
FEATURE [PartDesign::Mirrored] Mirrored003
  BaseFeature = -> Pad018
  MirrorPlane = -> Sketch026 [V_Axis]
  Originals = -> [Pad018]
FEATURE [PartDesign::Body] Body033  label="consolidator"
  Group = -> [ShapeBinder008,Sketch018,Pad013,Sketch026,Pad018,Mirrored003]
  Origin = -> Origin033
  Tip = -> Mirrored003
FEATURE [PartDesign::ShapeBinder] ShapeBinder012
  Support = -> [Fusion003]
  TraceSupport = false
FEATURE [Sketcher::SketchObject] Sketch027
  ExternalGeometry = -> [ShapeBinder012]
  FullyConstrained = false
  MapMode = 5
  Support = -> [XY_Plane037]
  sketch-geometry (13):
    g0: LineSegment StartX=-112.524 StartY=69.75 StartZ=0 EndX=-42.5237 EndY=69.75 EndZ=0
    g1: LineSegment StartX=-42.5237 StartY=69.75 StartZ=0 EndX=-22.55 EndY=49.7763 EndZ=0
    g2: LineSegment StartX=-22.55 StartY=49.7763 StartZ=0 EndX=22.55 EndY=49.7763 EndZ=0
    g3: LineSegment StartX=22.55 StartY=49.7763 StartZ=0 EndX=42.5237 EndY=69.75 EndZ=0
    g4: LineSegment StartX=42.5237 StartY=69.75 StartZ=0 EndX=112.524 EndY=69.75 EndZ=0
    g5: LineSegment StartX=112.524 StartY=69.75 StartZ=0 EndX=112.524 EndY=64.75 EndZ=0
    g6: LineSegment StartX=112.524 StartY=64.75 StartZ=0 EndX=44.5947 EndY=64.75 EndZ=0
    g7: LineSegment StartX=44.5947 StartY=64.75 StartZ=0 EndX=24.6211 EndY=44.7763 EndZ=0
    g8: LineSegment StartX=24.6211 StartY=44.7763 StartZ=0 EndX=-24.6211 EndY=44.7763 EndZ=0
    g9: LineSegment StartX=-24.6211 StartY=44.7763 StartZ=0 EndX=-44.5947 EndY=64.75 EndZ=0
    g10: LineSegment StartX=-44.5947 StartY=64.75 StartZ=0 EndX=-112.524 EndY=64.75 EndZ=0
    g11: LineSegment StartX=-112.524 StartY=64.75 StartZ=0 EndX=-112.524 EndY=69.75 EndZ=0
    g12: LineSegment StartX=30.8461 StartY=51.0013 StartZ=0 EndX=27.3105 EndY=54.5369 EndZ=0
  constraints (33):
    c: Coincident(g0,g-4)
    c: Coincident(g0,g1)
    c: Coincident(g1,g2)
    c: Coincident(g2,g-6)
    c: Coincident(g2,g3)
    c: Coincident(g3,g-7)
    c: Coincident(g3,g4)
    c: Coincident(g4,g5)
    c: Vertical(g5)
    c: Coincident(g5,g6)
    c: Horizontal(g6)
    c: Coincident(g6,g7)
    c: Coincident(g7,g8)
    c: Coincident(g8,g9)
    c: Coincident(g9,g10)
    c: Horizontal(g10)
    c: Coincident(g10,g11)
    c: Coincident(g11,g0)
    c: Vertical(g11)
    c: Coincident(g1,g-5)
    c: DistanceY(g11,g11) = 5
    c: Horizontal(g9,g6)
    c: Equal(g3,g7)
    c: Equal(g1,g9)
    c: Angle(g9) = 2.35619
    c: Symmetric(g8,g7,g-2)
    c: PointOnObject(g12,g7)
    c: PointOnObject(g12,g3)
    c: Perpendicular(g3,g12)
    c: Equal(g12,g5)
    c: PointOnObject(g0,g-9)
    c: Symmetric(g4,g0,g-2)
    c: DistanceX(g4,g4) = 70
FEATURE [PartDesign::Pad] Pad019
  Direction = (1,1,1)
  Length = 2
  Length2 = 100
  Profile = -> Sketch027
  Type = 0
FEATURE [PartDesign::Body] Body037  label="border-center"
  Group = -> [ShapeBinder012,Sketch027,Pad019]
  Origin = -> Origin037
  Placement = pos=(0,0,-2) rot=(0,0,1;0rad)
  Tip = -> Pad019
FEATURE [PartDesign::ShapeBinder] ShapeBinder013
  Placement = pos=(0,0,10) rot=(0,0,1;0rad)
  Support = -> [Body034]
  TraceSupport = false
FEATURE [Sketcher::SketchObject] Sketch029
  ExternalGeometry = -> [ShapeBinder013]
  FullyConstrained = false
  MapMode = 5
  Support = -> [XY_Plane038]
  sketch-geometry (2):
    g0: Circle CenterX=0 CenterY=18 CenterZ=0 NormalX=0 NormalY=0 NormalZ=1 AngleXU=0 Radius=13.4
    g1: LineSegment StartX=8.55101 StartY=28.317 StartZ=0 EndX=7.27474 EndY=26.7771 EndZ=0
  constraints (5):
    c: Coincident(g0,g-3)
    c: PointOnObject(g1,g0)
    c: PointOnObject(g1,g-3)
    c: Perpendicular(g0,g1)
    c: Distance(g1) = 2
FEATURE [PartDesign::Pad] Pad020
  Direction = (1,1,1)
  Length = 6
  Length2 = 100
  Profile = -> Sketch029
  Type = 0
FEATURE [Sketcher::SketchObject] Sketch030
  ExternalGeometry = -> [Pad020]
  FullyConstrained = true
  MapMode = 5
  Placement = pos=(0,0,6) rot=(0,0,1;0rad)
  Support = -> [Pad020]
  sketch-geometry (1):
    g0: Circle CenterX=0 CenterY=18 CenterZ=0 NormalX=0 NormalY=0 NormalZ=1 AngleXU=0 Radius=11.3
  constraints (2):
    c: Coincident(g0,g-3)
    c: Radius(g0) = 11.3
FEATURE [PartDesign::Pad] Pad021
  BaseFeature = -> Pad020
  Direction = (1,1,1)
  Length = 10
  Length2 = 100
  Profile = -> Sketch030
  Type = 0
FEATURE [Sketcher::SketchObject] Sketch031
  ExternalGeometry = -> [Pad021]
  FullyConstrained = false
  MapMode = 5
  Placement = pos=(0,0,16) rot=(0,0,1;0rad)
  Support = -> [Pad021]
  sketch-geometry (2):
    g0: Circle CenterX=0 CenterY=18 CenterZ=0 NormalX=0 NormalY=0 NormalZ=1 AngleXU=0 Radius=9.3
    g1: LineSegment StartX=5.57642 StartY=25.4427 StartZ=0 EndX=6.77565 EndY=27.0433 EndZ=0
  constraints (5):
    c: Coincident(g0,g-3)
    c: PointOnObject(g1,g0)
    c: PointOnObject(g1,g-3)
    c: Perpendicular(g-3,g1)
    c: Distance(g1) = 2
FEATURE [PartDesign::Pocket] Pocket008
  BaseFeature = -> Pad021
  Length = 5
  Length2 = 100
  Profile = -> Sketch031
  Type = 1
FEATURE [PartDesign::Body] Body038  label="panel-center-tube"
  Group = -> [ShapeBinder013,Sketch029,Pad020,Sketch030,Pad021,Sketch031,Pocket008]
  Origin = -> Origin038
  Placement = pos=(0,0,4) rot=(0,0,1;0rad)
  Tip = -> Pocket008
FEATURE [PartDesign::ShapeBinder] ShapeBinder014
  Placement = pos=(0,0,4) rot=(0,0,1;0rad)
  Support = -> [Body038]
  TraceSupport = false
FEATURE [Sketcher::SketchObject] Sketch032
  ExternalGeometry = -> [ShapeBinder014]
  FullyConstrained = false
  MapMode = 5
  Support = -> [XY_Plane039]
  sketch-geometry (2):
    g0: Circle CenterX=0 CenterY=18 CenterZ=0 NormalX=0 NormalY=0 NormalZ=1 AngleXU=0 Radius=12.4
    g1: LineSegment StartX=10.4868 StartY=22.2091 StartZ=0 EndX=11.5077 EndY=22.6189 EndZ=0
  constraints (5):
    c: Coincident(g0,g-3)
    c: PointOnObject(g1,g-3)
    c: PointOnObject(g1,g0)
    c: Perpendicular(g0,g1)
    c: Distance(g1) = 1.1
FEATURE [PartDesign::Pad] Pad022
  Direction = (1,1,1)
  Length = 10
  Length2 = 100
  Profile = -> Sketch032
  Type = 0
FEATURE [Sketcher::SketchObject] Sketch033
  ExternalGeometry = -> [Pad022]
  FullyConstrained = false
  MapMode = 5
  Placement = pos=(0,0,0) rot=(1,0,0;3.14159rad)
  Support = -> [Pad022]
  sketch-geometry (2):
    g0: Circle CenterX=0 CenterY=-18 CenterZ=0 NormalX=0 NormalY=0 NormalZ=1 AngleXU=0 Radius=11.4
    g1: LineSegment StartX=10.3858 StartY=-13.2995 StartZ=0 EndX=11.2968 EndY=-12.8871 EndZ=0
  constraints (5):
    c: Coincident(g0,g-3)
    c: PointOnObject(g1,g0)
    c: PointOnObject(g1,g-3)
    c: Perpendicular(g-3,g1)
    c: Distance(g1) = 1
FEATURE [PartDesign::Pocket] Pocket009
  BaseFeature = -> Pad022
  Length = 9
  Length2 = 100
  Profile = -> Sketch033
  Type = 0
FEATURE [Sketcher::SketchObject] Sketch034
  ExternalGeometry = -> [Pocket009]
  FullyConstrained = false
  MapMode = 5
  Placement = pos=(0,0,9) rot=(1,0,0;3.14159rad)
  Support = -> [Pocket009]
  sketch-geometry (2):
    g0: Circle CenterX=0 CenterY=-18 CenterZ=0 NormalX=0 NormalY=0 NormalZ=1 AngleXU=0 Radius=8.4
    g1: LineSegment StartX=6.88906 StartY=-13.1937 StartZ=0 EndX=9.34944 EndY=-11.4771 EndZ=0
  constraints (5):
    c: Coincident(g0,g-3)
    c: PointOnObject(g1,g0)
    c: PointOnObject(g1,g-3)
    c: Perpendicular(g-3,g1)
    c: Distance(g1) = 3
FEATURE [PartDesign::Pocket] Pocket010
  BaseFeature = -> Pocket009
  Length = 5
  Length2 = 100
  Profile = -> Sketch034
  Type = 0
FEATURE [PartDesign::Body] Body039  label="panel-center-tube-cap"
  Group = -> [ShapeBinder014,Sketch032,Pad022,Sketch033,Pocket009,Sketch034,Pocket010]
  Origin = -> Origin039
  Placement = pos=(0,0,11) rot=(0,0,1;0rad)
  Tip = -> Pocket010
FEATURE [PartDesign::ShapeBinder] ShapeBinder015
  Support = -> [Fusion003]
  TraceSupport = false
FEATURE [PartDesign::ShapeBinder] ShapeBinder016
  Placement = pos=(0,0,-2) rot=(0,0,1;0rad)
  Support = -> [Body037]
  TraceSupport = false
FEATURE [Sketcher::SketchObject] Sketch035
  ExternalGeometry = -> [ShapeBinder016,ShapeBinder015]
  FullyConstrained = false
  MapMode = 5
  Support = -> [XY_Plane040]
  sketch-geometry (21):
    g0: LineSegment StartX=-112.524 StartY=64.75 StartZ=0 EndX=-44.5947 EndY=64.75 EndZ=0
    g1: LineSegment StartX=-44.5947 StartY=64.75 StartZ=0 EndX=102.45 EndY=-49.3621 EndZ=0
    g2: LineSegment StartX=102.45 StartY=-49.3621 StartZ=0 EndX=42.9379 EndY=-68.75 EndZ=0
    g3: LineSegment StartX=42.9379 StartY=-68.75 StartZ=0 EndX=83.0621 EndY=-68.75 EndZ=0
    g4: LineSegment StartX=83.0621 StartY=-68.75 StartZ=0 EndX=97.3 EndY=-12.8 EndZ=0
    g5: LineSegment StartX=97.3 StartY=-12.8 StartZ=0 EndX=87.3 EndY=-12.8 EndZ=0
    g6: LineSegment StartX=87.3 StartY=-12.8 StartZ=0 EndX=97.3 EndY=-45.8 EndZ=0
    g7: LineSegment StartX=97.3 StartY=-45.8 StartZ=0 EndX=97.3 EndY=-12.8 EndZ=0
    g8: LineSegment StartX=223.588 StartY=-64.75 StartZ=0 EndX=-225.61 EndY=384.448 EndZ=0
    g9: LineSegment StartX=-225.61 StartY=384.448 StartZ=0 EndX=-225.61 EndY=-439.797 EndZ=0
    g10: LineSegment StartX=-225.61 StartY=-439.797 StartZ=0 EndX=214.186 EndY=0 EndZ=0
    g11: LineSegment StartX=214.186 StartY=0 StartZ=0 EndX=-225.61 EndY=439.797 EndZ=0
    g12: LineSegment StartX=-225.61 StartY=439.797 StartZ=0 EndX=-225.61 EndY=-384.448 EndZ=0
    g13: LineSegment StartX=-225.61 StartY=-384.448 StartZ=0 EndX=223.588 EndY=64.75 EndZ=0
    g14: LineSegment StartX=223.588 StartY=64.75 StartZ=0 EndX=-112.524 EndY=64.75 EndZ=0
    g15: LineSegment StartX=97.3 StartY=-12.8 StartZ=0 EndX=-112.524 EndY=-12.8 EndZ=0
    g16: LineSegment StartX=-112.524 StartY=-12.8 StartZ=0 EndX=-112.524 EndY=-64.75 EndZ=0
    g17: LineSegment StartX=-112.524 StartY=-64.75 StartZ=0 EndX=223.588 EndY=-64.75 EndZ=0
    g18: LineSegment StartX=218.834 StartY=59.9963 StartZ=0 EndX=239.876 EndY=-4.59159 EndZ=0
    g19: LineSegment StartX=143.095 StartY=167.158 StartZ=0 EndX=95.0617 EndY=119.125 EndZ=0
    g20: LineSegment StartX=-225.61 StartY=-68.75 StartZ=0 EndX=-157.681 EndY=-68.75 EndZ=0
  constraints (51):
    c: Coincident(g-3,g0)
    c: Coincident(g0,g-3)
    c: Coincident(g0,g1)
    c: Coincident(g1,g-6)
    c: Coincident(g1,g2)
    c: Coincident(g2,g-7)
    c: Coincident(g2,g3)
    c: Coincident(g3,g-8)
    c: Coincident(g3,g4)
    c: Coincident(g4,g-9)
    c: Coincident(g4,g5)
    c: Coincident(g5,g-10)
    c: Coincident(g5,g6)
    c: Coincident(g6,g-11)
    c: Coincident(g6,g7)
    c: Coincident(g8,g9)
    c: Vertical(g9)
    c: Coincident(g9,g10)
    c: PointOnObject(g10,g-1)
    c: Coincident(g10,g11)
    c: Coincident(g11,g12)
    c: Coincident(g12,g13)
    c: Coincident(g13,g14)
    c: Coincident(g14,g0)
    c: Horizontal(g14)
    c: Coincident(g7,g15)
    c: Horizontal(g15)
    c: Coincident(g15,g16)
    c: Vertical(g16)
    c: Coincident(g16,g17)
    c: Coincident(g17,g8)
    c: Horizontal(g17)
    c: Vertical(g16,g0)
    c: PointOnObject(g18,g13)
    c: PointOnObject(g18,g2)
    c: Perpendicular(g18,g2)
    c: Equal(g18,g0)
    c: PointOnObject(g19,g4)
    c: PointOnObject(g19,g11)
    c: Perpendicular(g11,g19)
    c: Equal(g19,g18)
    c: PointOnObject(g20,g12)
    c: PointOnObject(g20,g3)
    c: Horizontal(g20)
    c: Equal(g20,g19)
    c: Angle(g11) = 2.35619
    c: Angle(g13) = 0.785398
    c: Symmetric(g9,g11,g-1)
    c: Coincident(g7,g-11)
    c: Symmetric(g12,g8,g-1)
    c: Symmetric(g8,g13,g-1)
FEATURE [PartDesign::Pad] Pad023
  Direction = (1,1,1)
  Length = 2
  Length2 = 100
  Profile = -> Sketch035
  Reversed = true
  Type = 0
FEATURE [PartDesign::Body] Body040  label="border-side"
  Group = -> [ShapeBinder015,ShapeBinder016,Sketch035,Pad023]
  Origin = -> Origin040
  Tip = -> Pad023
FEATURE [PartDesign::ShapeBinder] ShapeBinder017
  Support = -> [Fusion003]
  TraceSupport = false
FEATURE [PartDesign::ShapeBinder] ShapeBinder018
  Support = -> [Body033]
  TraceSupport = false
FEATURE [Sketcher::SketchObject] Sketch036
  ExternalGeometry = -> [ShapeBinder017,ShapeBinder018]
  FullyConstrained = false
  MapMode = 5
  Support = -> [XY_Plane041]
  sketch-geometry (18):
    g0: LineSegment StartX=-83.5385 StartY=69.9 StartZ=0 EndX=-83.5385 EndY=-69.9 EndZ=0
    g1: LineSegment StartX=-83.5385 StartY=-69.9 StartZ=0 EndX=-42.4615 EndY=-69.9 EndZ=0
    g2: LineSegment StartX=-42.4615 StartY=-69.9 StartZ=0 EndX=-22.4 EndY=-49.8385 EndZ=0
    g3: LineSegment StartX=22.4 StartY=-49.8385 StartZ=0 EndX=42.4615 EndY=-69.9 EndZ=0
    g4: LineSegment StartX=42.4615 StartY=-69.9 StartZ=0 EndX=83.5385 EndY=-69.9 EndZ=0
    g5: LineSegment StartX=83.5385 StartY=-69.9 StartZ=0 EndX=83.5385 EndY=69.9 EndZ=0
    g6: LineSegment StartX=83.5385 StartY=69.9 StartZ=0 EndX=42.4615 EndY=69.9 EndZ=0
    g7: LineSegment StartX=42.4615 StartY=69.9 StartZ=0 EndX=22.4 EndY=49.8385 EndZ=0
    g8: LineSegment StartX=22.4 StartY=49.8385 StartZ=0 EndX=-22.4 EndY=49.8385 EndZ=0
    g9: LineSegment StartX=-22.4 StartY=49.8385 StartZ=0 EndX=-42.4615 EndY=69.9 EndZ=0
    g10: LineSegment StartX=-42.4615 StartY=69.9 StartZ=0 EndX=-83.5385 EndY=69.9 EndZ=0
    g11: GeomPoint X=-10 Y=-49.8385 Z=0
    g12: GeomPoint X=10 Y=-49.8385 Z=0
    g13: LineSegment StartX=22.4 StartY=-49.8385 StartZ=0 EndX=10 EndY=-49.8385 EndZ=0
    g14: LineSegment StartX=-10 StartY=-49.8385 StartZ=0 EndX=-22.4 EndY=-49.8385 EndZ=0
    g15: LineSegment StartX=-10 StartY=15 StartZ=0 EndX=10 EndY=15 EndZ=0
    g16: LineSegment StartX=10 StartY=-49.8385 StartZ=0 EndX=10 EndY=15 EndZ=0
    g17: LineSegment StartX=-10 StartY=15 StartZ=0 EndX=-10 EndY=-49.8385 EndZ=0
  constraints (36):
    c: Coincident(g-4,g0)
    c: Coincident(g0,g-24)
    c: Coincident(g0,g1)
    c: Coincident(g1,g-23)
    c: Coincident(g1,g2)
    c: Coincident(g2,g-22)
    c: Coincident(g3,g-20)
    c: Coincident(g3,g4)
    c: Coincident(g4,g-19)
    c: Coincident(g4,g5)
    c: Coincident(g5,g-9)
    c: Coincident(g5,g6)
    c: Coincident(g6,g-8)
    c: Coincident(g6,g7)
    c: Coincident(g7,g-7)
    c: Coincident(g7,g8)
    c: Coincident(g8,g-6)
    c: Coincident(g8,g9)
    c: Coincident(g9,g-5)
    c: Coincident(g9,g10)
    c: Coincident(g10,g0)
    c: Symmetric(g11,g12,g-2)
    c: Coincident(g13,g3)
    c: Coincident(g13,g12)
    c: Coincident(g14,g11)
    c: Coincident(g14,g2)
    c: Symmetric(g15,g15,g-2)
    c: Vertical(g15,g14)
    c: Coincident(g3,g-21)
    c: Coincident(g16,g13)
    c: Coincident(g16,g15)
    c: Coincident(g17,g15)
    c: Coincident(g17,g14)
    c: PointOnObject(g14,g-21)
    c: DistanceX(g15,g15) = 20
    c: PointOnObject(g15,g-33)
FEATURE [PartDesign::Pad] Pad024
  Direction = (1,1,1)
  Length = 2
  Length2 = 100
  Profile = -> Sketch036
  Type = 0
FEATURE [PartDesign::Body] Body041
  Group = -> [ShapeBinder017,Sketch036,ShapeBinder018,Pad024]
  Origin = -> Origin041
  Placement = pos=(0,0,-7) rot=(0,0,1;0rad)
  Tip = -> Pad024
